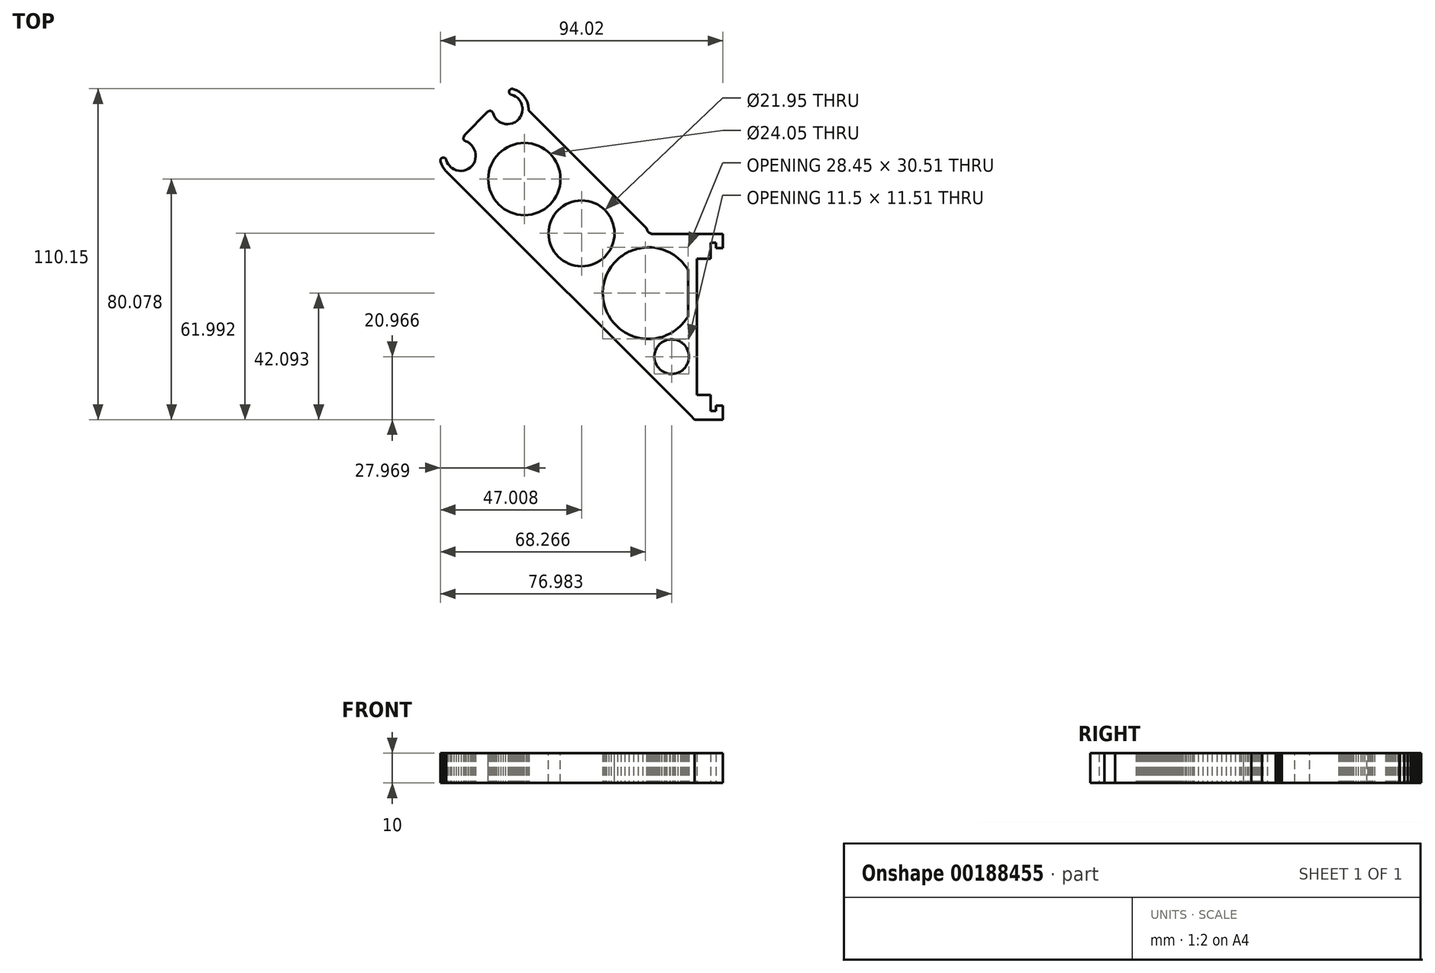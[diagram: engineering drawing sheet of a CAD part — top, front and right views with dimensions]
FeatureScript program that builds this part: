
annotation { "Feature Type Name" : "Feature", "Feature Type Description" : "" }
export const myFeature = defineFeature(function(context is Context, id is Id, definition is map)
    precondition{}
    {
        {
            var Q0;
            Q0=qCreatedBy(makeId("Top.planeOp"),FACE);
            var sketch = newSketch(context, id + "F0", { "sketchPlane" : qUnion([Q0])});
            skLineSegment(sketch, "E0", {"start": v(3.2, -2.47) * mm, "end": v(3.28, -2.4) * mm});
            skLineSegment(sketch, "E1", {"start": v(3.28, -2.4) * mm, "end": v(3.32, -2.36) * mm});
            skLineSegment(sketch, "E2", {"start": v(3.32, -2.36) * mm, "end": v(3.4, -2.28) * mm});
            skLineSegment(sketch, "E3", {"start": v(3.4, -2.28) * mm, "end": v(3.42, -2.25) * mm});
            skLineSegment(sketch, "E4", {"start": v(3.42, -2.25) * mm, "end": v(3.49, -2.16) * mm});
            skLineSegment(sketch, "E5", {"start": v(3.49, -2.16) * mm, "end": v(3.52, -2.12) * mm});
            skLineSegment(sketch, "E6", {"start": v(3.52, -2.12) * mm, "end": v(3.54, -2.07) * mm});
            skLineSegment(sketch, "E7", {"start": v(3.54, -2.07) * mm, "end": v(3.55, -2.06) * mm});
            skLineSegment(sketch, "E8", {"start": v(3.55, -2.06) * mm, "end": v(3.55, -2.03) * mm});
            skLineSegment(sketch, "E9", {"start": v(3.55, -2.03) * mm, "end": v(3.55, -1.98) * mm});
            skLineSegment(sketch, "E10", {"start": v(3.55, -1.98) * mm, "end": v(3.55, -1.8) * mm});
            skLineSegment(sketch, "E11", {"start": v(3.55, -1.8) * mm, "end": v(3.55, -1.76) * mm});
            skLineSegment(sketch, "E12", {"start": v(3.55, -1.76) * mm, "end": v(3.55, -1.72) * mm});
            skLineSegment(sketch, "E13", {"start": v(3.55, -1.72) * mm, "end": v(3.55, -1.7) * mm});
            skLineSegment(sketch, "E14", {"start": v(3.55, -1.7) * mm, "end": v(3.55, -1.66) * mm});
            skLineSegment(sketch, "E15", {"start": v(3.55, -1.66) * mm, "end": v(3.55, -1.65) * mm});
            skLineSegment(sketch, "E16", {"start": v(3.55, -1.65) * mm, "end": v(3.55, -1.63) * mm});
            skLineSegment(sketch, "E17", {"start": v(3.55, -1.63) * mm, "end": v(3.55, -1.62) * mm});
            skLineSegment(sketch, "E18", {"start": v(3.55, -1.62) * mm, "end": v(3.55, -1.62) * mm});
            skLineSegment(sketch, "E19", {"start": v(3.55, -1.62) * mm, "end": v(3.55, -1.56) * mm});
            skLineSegment(sketch, "E20", {"start": v(3.55, -1.56) * mm, "end": v(3.55, -1.56) * mm});
            skLineSegment(sketch, "E21", {"start": v(3.55, -1.56) * mm, "end": v(3.55, -1.55) * mm});
            skLineSegment(sketch, "E22", {"start": v(3.55, -1.55) * mm, "end": v(3.55, -1.48) * mm});
            skLineSegment(sketch, "E23", {"start": v(3.55, -1.48) * mm, "end": v(3.55, -1.42) * mm});
            skLineSegment(sketch, "E24", {"start": v(3.55, -1.42) * mm, "end": v(3.55, -1.36) * mm});
            skLineSegment(sketch, "E25", {"start": v(3.55, -1.36) * mm, "end": v(3.55, -1.2) * mm});
            skLineSegment(sketch, "E26", {"start": v(3.55, -1.2) * mm, "end": v(3.55, -1.17) * mm});
            skLineSegment(sketch, "E27", {"start": v(3.55, -1.17) * mm, "end": v(3.55, -0.86) * mm});
            skLineSegment(sketch, "E28", {"start": v(3.55, -0.86) * mm, "end": v(3.55, -0.53) * mm});
            skLineSegment(sketch, "E29", {"start": v(3.55, -0.53) * mm, "end": v(3.53, -0.5) * mm});
            skLineSegment(sketch, "E30", {"start": v(3.53, -0.5) * mm, "end": v(3.52, -0.48) * mm});
            skLineSegment(sketch, "E31", {"start": v(3.52, -0.48) * mm, "end": v(3.46, -0.4) * mm});
            skLineSegment(sketch, "E32", {"start": v(3.46, -0.4) * mm, "end": v(3.42, -0.35) * mm});
            skLineSegment(sketch, "E33", {"start": v(3.42, -0.35) * mm, "end": v(3.36, -0.27) * mm});
            skLineSegment(sketch, "E34", {"start": v(3.36, -0.27) * mm, "end": v(3.32, -0.23) * mm});
            skLineSegment(sketch, "E35", {"start": v(3.32, -0.23) * mm, "end": v(3.24, -0.16) * mm});
            skLineSegment(sketch, "E36", {"start": v(3.24, -0.16) * mm, "end": v(3.2, -0.13) * mm});
            skLineSegment(sketch, "E37", {"start": v(3.2, -0.13) * mm, "end": v(3.12, -0.06) * mm});
            skLineSegment(sketch, "E38", {"start": v(3.12, -0.06) * mm, "end": v(3.08, -0.03) * mm});
            skLineSegment(sketch, "E39", {"start": v(3.08, -0.03) * mm, "end": v(2.99, 0.02) * mm});
            skLineSegment(sketch, "E40", {"start": v(2.99, 0.02) * mm, "end": v(2.95, 0.05) * mm});
            skLineSegment(sketch, "E41", {"start": v(2.95, 0.05) * mm, "end": v(2.85, 0.1) * mm});
            skLineSegment(sketch, "E42", {"start": v(2.85, 0.1) * mm, "end": v(2.8, 0.12) * mm});
            skLineSegment(sketch, "E43", {"start": v(2.8, 0.12) * mm, "end": v(2.7, 0.15) * mm});
            skLineSegment(sketch, "E44", {"start": v(2.7, 0.15) * mm, "end": v(2.65, 0.17) * mm});
            skLineSegment(sketch, "E45", {"start": v(2.65, 0.17) * mm, "end": v(2.55, 0.2) * mm});
            skLineSegment(sketch, "E46", {"start": v(2.55, 0.2) * mm, "end": v(2.5, 0.2) * mm});
            skLineSegment(sketch, "E47", {"start": v(2.5, 0.2) * mm, "end": v(2.4, 0.22) * mm});
            skLineSegment(sketch, "E48", {"start": v(2.4, 0.22) * mm, "end": v(2.35, 0.22) * mm});
            skLineSegment(sketch, "E49", {"start": v(2.35, 0.22) * mm, "end": v(2.24, 0.23) * mm});
            skLineSegment(sketch, "E50", {"start": v(2.24, 0.23) * mm, "end": v(2.19, 0.23) * mm});
            skLineSegment(sketch, "E51", {"start": v(2.19, 0.23) * mm, "end": v(2.08, 0.22) * mm});
            skLineSegment(sketch, "E52", {"start": v(2.08, 0.22) * mm, "end": v(2.03, 0.22) * mm});
            skLineSegment(sketch, "E53", {"start": v(2.03, 0.22) * mm, "end": v(1.93, 0.2) * mm});
            skLineSegment(sketch, "E54", {"start": v(1.93, 0.2) * mm, "end": v(1.88, 0.19) * mm});
            skLineSegment(sketch, "E55", {"start": v(1.88, 0.19) * mm, "end": v(1.78, 0.16) * mm});
            skLineSegment(sketch, "E56", {"start": v(1.78, 0.16) * mm, "end": v(1.73, 0.14) * mm});
            skLineSegment(sketch, "E57", {"start": v(1.73, 0.14) * mm, "end": v(1.63, 0.1) * mm});
            skLineSegment(sketch, "E58", {"start": v(1.63, 0.1) * mm, "end": v(1.58, 0.08) * mm});
            skLineSegment(sketch, "E59", {"start": v(1.58, 0.08) * mm, "end": v(1.49, 0.03) * mm});
            skLineSegment(sketch, "E60", {"start": v(1.49, 0.03) * mm, "end": v(1.44, 0) * mm});
            skLineSegment(sketch, "E61", {"start": v(1.44, 0) * mm, "end": v(1.36, -0.05) * mm});
            skLineSegment(sketch, "E62", {"start": v(1.36, -0.05) * mm, "end": v(1.31, -0.08) * mm});
            skLineSegment(sketch, "E63", {"start": v(1.31, -0.08) * mm, "end": v(1.23, -0.15) * mm});
            skLineSegment(sketch, "E64", {"start": v(1.23, -0.15) * mm, "end": v(1.2, -0.18) * mm});
            skLineSegment(sketch, "E65", {"start": v(1.2, -0.18) * mm, "end": v(1.12, -0.25) * mm});
            skLineSegment(sketch, "E66", {"start": v(1.12, -0.25) * mm, "end": v(1.08, -0.3) * mm});
            skLineSegment(sketch, "E67", {"start": v(1.08, -0.3) * mm, "end": v(1.02, -0.37) * mm});
            skLineSegment(sketch, "E68", {"start": v(1.02, -0.37) * mm, "end": v(0.99, -0.41) * mm});
            skLineSegment(sketch, "E69", {"start": v(0.99, -0.41) * mm, "end": v(0.93, -0.5) * mm});
            skLineSegment(sketch, "E70", {"start": v(0.93, -0.5) * mm, "end": v(0.9, -0.55) * mm});
            skLineSegment(sketch, "E71", {"start": v(0.9, -0.55) * mm, "end": v(0.85, -0.64) * mm});
            skLineSegment(sketch, "E72", {"start": v(0.85, -0.64) * mm, "end": v(0.83, -0.69) * mm});
            skLineSegment(sketch, "E73", {"start": v(0.83, -0.69) * mm, "end": v(0.8, -0.79) * mm});
            skLineSegment(sketch, "E74", {"start": v(0.8, -0.79) * mm, "end": v(0.78, -0.83) * mm});
            skLineSegment(sketch, "E75", {"start": v(0.78, -0.83) * mm, "end": v(0.75, -0.94) * mm});
            skLineSegment(sketch, "E76", {"start": v(0.75, -0.94) * mm, "end": v(0.74, -0.99) * mm});
            skLineSegment(sketch, "E77", {"start": v(0.74, -0.99) * mm, "end": v(0.72, -1.1) * mm});
            skLineSegment(sketch, "E78", {"start": v(0.72, -1.1) * mm, "end": v(0.71, -1.14) * mm});
            skLineSegment(sketch, "E79", {"start": v(0.71, -1.14) * mm, "end": v(0.7, -1.25) * mm});
            skLineSegment(sketch, "E80", {"start": v(0.7, -1.25) * mm, "end": v(0.7, -1.3) * mm});
            skLineSegment(sketch, "E81", {"start": v(0.7, -1.3) * mm, "end": v(0.7, -1.4) * mm});
            skLineSegment(sketch, "E82", {"start": v(0.7, -1.4) * mm, "end": v(0.71, -1.46) * mm});
            skLineSegment(sketch, "E83", {"start": v(0.71, -1.46) * mm, "end": v(0.73, -1.56) * mm});
            skLineSegment(sketch, "E84", {"start": v(0.73, -1.56) * mm, "end": v(0.74, -1.61) * mm});
            skLineSegment(sketch, "E85", {"start": v(0.74, -1.61) * mm, "end": v(0.76, -1.71) * mm});
            skLineSegment(sketch, "E86", {"start": v(0.76, -1.71) * mm, "end": v(0.78, -1.76) * mm});
            skLineSegment(sketch, "E87", {"start": v(0.78, -1.76) * mm, "end": v(0.81, -1.86) * mm});
            skLineSegment(sketch, "E88", {"start": v(0.81, -1.86) * mm, "end": v(0.83, -1.9) * mm});
            skLineSegment(sketch, "E89", {"start": v(0.83, -1.9) * mm, "end": v(0.88, -2) * mm});
            skLineSegment(sketch, "E90", {"start": v(0.88, -2) * mm, "end": v(0.9, -2.05) * mm});
            skLineSegment(sketch, "E91", {"start": v(0.9, -2.05) * mm, "end": v(0.96, -2.14) * mm});
            skLineSegment(sketch, "E92", {"start": v(0.96, -2.14) * mm, "end": v(0.99, -2.18) * mm});
            skLineSegment(sketch, "E93", {"start": v(0.99, -2.18) * mm, "end": v(1.05, -2.26) * mm});
            skLineSegment(sketch, "E94", {"start": v(1.05, -2.26) * mm, "end": v(1.08, -2.3) * mm});
            skLineSegment(sketch, "E95", {"start": v(1.08, -2.3) * mm, "end": v(1.16, -2.38) * mm});
            skLineSegment(sketch, "E96", {"start": v(1.16, -2.38) * mm, "end": v(1.2, -2.42) * mm});
            skLineSegment(sketch, "E97", {"start": v(1.2, -2.42) * mm, "end": v(1.27, -2.49) * mm});
            skLineSegment(sketch, "E98", {"start": v(1.27, -2.49) * mm, "end": v(1.31, -2.52) * mm});
            skLineSegment(sketch, "E99", {"start": v(1.31, -2.52) * mm, "end": v(1.4, -2.58) * mm});
            skLineSegment(sketch, "E100", {"start": v(1.4, -2.58) * mm, "end": v(1.44, -2.6) * mm});
            skLineSegment(sketch, "E101", {"start": v(1.44, -2.6) * mm, "end": v(1.54, -2.66) * mm});
            skLineSegment(sketch, "E102", {"start": v(1.54, -2.66) * mm, "end": v(1.58, -2.68) * mm});
            skLineSegment(sketch, "E103", {"start": v(1.58, -2.68) * mm, "end": v(1.68, -2.72) * mm});
            skLineSegment(sketch, "E104", {"start": v(1.68, -2.72) * mm, "end": v(1.73, -2.74) * mm});
            skLineSegment(sketch, "E105", {"start": v(1.73, -2.74) * mm, "end": v(1.83, -2.77) * mm});
            skLineSegment(sketch, "E106", {"start": v(1.83, -2.77) * mm, "end": v(1.88, -2.78) * mm});
            skLineSegment(sketch, "E107", {"start": v(1.88, -2.78) * mm, "end": v(1.98, -2.8) * mm});
            skLineSegment(sketch, "E108", {"start": v(1.98, -2.8) * mm, "end": v(2.03, -2.81) * mm});
            skLineSegment(sketch, "E109", {"start": v(2.03, -2.81) * mm, "end": v(2.14, -2.82) * mm});
            skLineSegment(sketch, "E110", {"start": v(2.14, -2.82) * mm, "end": v(2.19, -2.82) * mm});
            skLineSegment(sketch, "E111", {"start": v(2.19, -2.82) * mm, "end": v(2.3, -2.82) * mm});
            skLineSegment(sketch, "E112", {"start": v(2.3, -2.82) * mm, "end": v(2.35, -2.82) * mm});
            skLineSegment(sketch, "E113", {"start": v(2.35, -2.82) * mm, "end": v(2.45, -2.8) * mm});
            skLineSegment(sketch, "E114", {"start": v(2.45, -2.8) * mm, "end": v(2.5, -2.8) * mm});
            skLineSegment(sketch, "E115", {"start": v(2.5, -2.8) * mm, "end": v(2.6, -2.78) * mm});
            skLineSegment(sketch, "E116", {"start": v(2.6, -2.78) * mm, "end": v(2.65, -2.76) * mm});
            skLineSegment(sketch, "E117", {"start": v(2.65, -2.76) * mm, "end": v(2.75, -2.73) * mm});
            skLineSegment(sketch, "E118", {"start": v(2.75, -2.73) * mm, "end": v(2.8, -2.71) * mm});
            skLineSegment(sketch, "E119", {"start": v(2.8, -2.71) * mm, "end": v(2.9, -2.67) * mm});
            skLineSegment(sketch, "E120", {"start": v(2.9, -2.67) * mm, "end": v(2.95, -2.65) * mm});
            skLineSegment(sketch, "E121", {"start": v(2.95, -2.65) * mm, "end": v(3.04, -2.6) * mm});
            skLineSegment(sketch, "E122", {"start": v(3.04, -2.6) * mm, "end": v(3.08, -2.56) * mm});
            skLineSegment(sketch, "E123", {"start": v(3.08, -2.56) * mm, "end": v(3.16, -2.5) * mm});
            skLineSegment(sketch, "E124", {"start": v(3.16, -2.5) * mm, "end": v(3.2, -2.47) * mm});
            skLineSegment(sketch, "E125", {"start": v(2.16, 0.86) * mm, "end": v(2.17, 0.83) * mm});
            skLineSegment(sketch, "E126", {"start": v(2.17, 0.83) * mm, "end": v(2.17, 0.83) * mm});
            skLineSegment(sketch, "E127", {"start": v(2.17, 0.83) * mm, "end": v(2.18, 0.8) * mm});
            skLineSegment(sketch, "E128", {"start": v(2.18, 0.8) * mm, "end": v(2.19, 0.8) * mm});
            skLineSegment(sketch, "E129", {"start": v(2.19, 0.8) * mm, "end": v(2.2, 0.76) * mm});
            skLineSegment(sketch, "E130", {"start": v(2.2, 0.76) * mm, "end": v(2.2, 0.76) * mm});
            skLineSegment(sketch, "E131", {"start": v(2.2, 0.76) * mm, "end": v(2.23, 0.74) * mm});
            skLineSegment(sketch, "E132", {"start": v(2.23, 0.74) * mm, "end": v(2.23, 0.73) * mm});
            skLineSegment(sketch, "E133", {"start": v(2.23, 0.73) * mm, "end": v(2.25, 0.71) * mm});
            skLineSegment(sketch, "E134", {"start": v(2.25, 0.71) * mm, "end": v(2.26, 0.71) * mm});
            skLineSegment(sketch, "E135", {"start": v(2.26, 0.71) * mm, "end": v(2.29, 0.7) * mm});
            skLineSegment(sketch, "E136", {"start": v(2.29, 0.7) * mm, "end": v(2.29, 0.7) * mm});
            skLineSegment(sketch, "E137", {"start": v(2.29, 0.7) * mm, "end": v(2.32, 0.68) * mm});
            skLineSegment(sketch, "E138", {"start": v(2.32, 0.68) * mm, "end": v(2.32, 0.68) * mm});
            skLineSegment(sketch, "E139", {"start": v(2.32, 0.68) * mm, "end": v(2.35, 0.67) * mm});
            skLineSegment(sketch, "E140", {"start": v(2.35, 0.67) * mm, "end": v(2.36, 0.67) * mm});
            skLineSegment(sketch, "E141", {"start": v(2.36, 0.67) * mm, "end": v(2.4, 0.67) * mm});
            skLineSegment(sketch, "E142", {"start": v(2.4, 0.67) * mm, "end": v(2.47, 0.67) * mm});
            skLineSegment(sketch, "E143", {"start": v(2.47, 0.67) * mm, "end": v(4.7, 0.67) * mm});
            skLineSegment(sketch, "E144", {"start": v(4.7, 0.67) * mm, "end": v(4.7, 0.65) * mm});
            skLineSegment(sketch, "E145", {"start": v(4.7, 0.65) * mm, "end": v(4.7, 0.2) * mm});
            skLineSegment(sketch, "E146", {"start": v(4.7, 0.2) * mm, "end": v(4.7, 0.2) * mm});
            skLineSegment(sketch, "E147", {"start": v(4.7, 0.2) * mm, "end": v(4.48, 0.2) * mm});
            skLineSegment(sketch, "E148", {"start": v(4.48, 0.2) * mm, "end": v(4.48, 0.21) * mm});
            skLineSegment(sketch, "E149", {"start": v(4.48, 0.21) * mm, "end": v(4.48, 0.38) * mm});
            skLineSegment(sketch, "E150", {"start": v(4.48, 0.38) * mm, "end": v(4.47, 0.38) * mm});
            skLineSegment(sketch, "E151", {"start": v(4.47, 0.38) * mm, "end": v(4.3, 0.38) * mm});
            skLineSegment(sketch, "E152", {"start": v(4.3, 0.38) * mm, "end": v(4.3, 0.36) * mm});
            skLineSegment(sketch, "E153", {"start": v(4.3, 0.36) * mm, "end": v(4.3, 0.18) * mm});
            skLineSegment(sketch, "E154", {"start": v(4.3, 0.18) * mm, "end": v(4.3, -0.15) * mm});
            skLineSegment(sketch, "E155", {"start": v(4.3, -0.15) * mm, "end": v(3.97, -0.15) * mm});
            skLineSegment(sketch, "E156", {"start": v(3.97, -0.15) * mm, "end": v(3.83, -0.15) * mm});
            skLineSegment(sketch, "E157", {"start": v(3.83, -0.15) * mm, "end": v(3.83, -3.22) * mm});
            skLineSegment(sketch, "E158", {"start": v(3.83, -3.22) * mm, "end": v(3.83, -4.69) * mm});
            skLineSegment(sketch, "E159", {"start": v(3.83, -4.69) * mm, "end": v(4.17, -4.69) * mm});
            skLineSegment(sketch, "E160", {"start": v(4.17, -4.69) * mm, "end": v(4.3, -4.69) * mm});
            skLineSegment(sketch, "E161", {"start": v(4.3, -4.69) * mm, "end": v(4.3, -5.02) * mm});
            skLineSegment(sketch, "E162", {"start": v(4.3, -5.02) * mm, "end": v(4.3, -5.2) * mm});
            skLineSegment(sketch, "E163", {"start": v(4.3, -5.2) * mm, "end": v(4.3, -5.22) * mm});
            skLineSegment(sketch, "E164", {"start": v(4.3, -5.22) * mm, "end": v(4.3, -5.22) * mm});
            skLineSegment(sketch, "E165", {"start": v(4.3, -5.22) * mm, "end": v(4.48, -5.22) * mm});
            skLineSegment(sketch, "E166", {"start": v(4.48, -5.22) * mm, "end": v(4.48, -5.21) * mm});
            skLineSegment(sketch, "E167", {"start": v(4.48, -5.21) * mm, "end": v(4.48, -5.04) * mm});
            skLineSegment(sketch, "E168", {"start": v(4.48, -5.04) * mm, "end": v(4.48, -5.04) * mm});
            skLineSegment(sketch, "E169", {"start": v(4.48, -5.04) * mm, "end": v(4.7, -5.04) * mm});
            skLineSegment(sketch, "E170", {"start": v(4.7, -5.04) * mm, "end": v(4.7, -5.06) * mm});
            skLineSegment(sketch, "E171", {"start": v(4.7, -5.06) * mm, "end": v(4.7, -5.5) * mm});
            skLineSegment(sketch, "E172", {"start": v(4.7, -5.5) * mm, "end": v(4.67, -5.5) * mm});
            skLineSegment(sketch, "E173", {"start": v(4.67, -5.5) * mm, "end": v(3.76, -5.5) * mm});
            skLineSegment(sketch, "E174", {"start": v(3.76, -5.5) * mm, "end": v(3.62, -5.36) * mm});
            skLineSegment(sketch, "E175", {"start": v(3.62, -5.36) * mm, "end": v(-4.5, 2.76) * mm});
            skLineSegment(sketch, "E176", {"start": v(2.42, -3.38) * mm, "end": v(2.43, -3.32) * mm});
            skLineSegment(sketch, "E177", {"start": v(2.43, -3.32) * mm, "end": v(2.44, -3.29) * mm});
            skLineSegment(sketch, "E178", {"start": v(2.44, -3.29) * mm, "end": v(2.45, -3.23) * mm});
            skLineSegment(sketch, "E179", {"start": v(2.45, -3.23) * mm, "end": v(2.46, -3.2) * mm});
            skLineSegment(sketch, "E180", {"start": v(2.46, -3.2) * mm, "end": v(2.49, -3.14) * mm});
            skLineSegment(sketch, "E181", {"start": v(2.49, -3.14) * mm, "end": v(2.5, -3.12) * mm});
            skLineSegment(sketch, "E182", {"start": v(2.5, -3.12) * mm, "end": v(2.54, -3.06) * mm});
            skLineSegment(sketch, "E183", {"start": v(2.54, -3.06) * mm, "end": v(2.56, -3.04) * mm});
            skLineSegment(sketch, "E184", {"start": v(2.56, -3.04) * mm, "end": v(2.6, -3) * mm});
            skLineSegment(sketch, "E185", {"start": v(2.6, -3) * mm, "end": v(2.62, -2.98) * mm});
            skLineSegment(sketch, "E186", {"start": v(2.62, -2.98) * mm, "end": v(2.67, -2.94) * mm});
            skLineSegment(sketch, "E187", {"start": v(2.67, -2.94) * mm, "end": v(2.7, -2.92) * mm});
            skLineSegment(sketch, "E188", {"start": v(2.7, -2.92) * mm, "end": v(2.75, -2.9) * mm});
            skLineSegment(sketch, "E189", {"start": v(2.75, -2.9) * mm, "end": v(2.78, -2.88) * mm});
            skLineSegment(sketch, "E190", {"start": v(2.78, -2.88) * mm, "end": v(2.84, -2.86) * mm});
            skLineSegment(sketch, "E191", {"start": v(2.84, -2.86) * mm, "end": v(2.87, -2.85) * mm});
            skLineSegment(sketch, "E192", {"start": v(2.87, -2.85) * mm, "end": v(2.93, -2.84) * mm});
            skLineSegment(sketch, "E193", {"start": v(2.93, -2.84) * mm, "end": v(2.96, -2.84) * mm});
            skLineSegment(sketch, "E194", {"start": v(2.96, -2.84) * mm, "end": v(3.02, -2.84) * mm});
            skLineSegment(sketch, "E195", {"start": v(3.02, -2.84) * mm, "end": v(3.05, -2.84) * mm});
            skLineSegment(sketch, "E196", {"start": v(3.05, -2.84) * mm, "end": v(3.11, -2.85) * mm});
            skLineSegment(sketch, "E197", {"start": v(3.11, -2.85) * mm, "end": v(3.14, -2.86) * mm});
            skLineSegment(sketch, "E198", {"start": v(3.14, -2.86) * mm, "end": v(3.2, -2.87) * mm});
            skLineSegment(sketch, "E199", {"start": v(3.2, -2.87) * mm, "end": v(3.23, -2.89) * mm});
            skLineSegment(sketch, "E200", {"start": v(3.23, -2.89) * mm, "end": v(3.29, -2.91) * mm});
            skLineSegment(sketch, "E201", {"start": v(3.29, -2.91) * mm, "end": v(3.31, -2.93) * mm});
            skLineSegment(sketch, "E202", {"start": v(3.31, -2.93) * mm, "end": v(3.36, -2.96) * mm});
            skLineSegment(sketch, "E203", {"start": v(3.36, -2.96) * mm, "end": v(3.38, -2.99) * mm});
            skLineSegment(sketch, "E204", {"start": v(3.38, -2.99) * mm, "end": v(3.43, -3.03) * mm});
            skLineSegment(sketch, "E205", {"start": v(3.43, -3.03) * mm, "end": v(3.45, -3.05) * mm});
            skLineSegment(sketch, "E206", {"start": v(3.45, -3.05) * mm, "end": v(3.49, -3.1) * mm});
            skLineSegment(sketch, "E207", {"start": v(3.49, -3.1) * mm, "end": v(3.5, -3.13) * mm});
            skLineSegment(sketch, "E208", {"start": v(3.5, -3.13) * mm, "end": v(3.53, -3.19) * mm});
            skLineSegment(sketch, "E209", {"start": v(3.53, -3.19) * mm, "end": v(3.54, -3.21) * mm});
            skLineSegment(sketch, "E210", {"start": v(3.54, -3.21) * mm, "end": v(3.56, -3.27) * mm});
            skLineSegment(sketch, "E211", {"start": v(3.56, -3.27) * mm, "end": v(3.56, -3.3) * mm});
            skLineSegment(sketch, "E212", {"start": v(3.56, -3.3) * mm, "end": v(3.57, -3.36) * mm});
            skLineSegment(sketch, "E213", {"start": v(3.57, -3.36) * mm, "end": v(3.57, -3.4) * mm});
            skLineSegment(sketch, "E214", {"start": v(3.57, -3.4) * mm, "end": v(3.57, -3.46) * mm});
            skLineSegment(sketch, "E215", {"start": v(3.57, -3.46) * mm, "end": v(3.57, -3.49) * mm});
            skLineSegment(sketch, "E216", {"start": v(3.57, -3.49) * mm, "end": v(3.56, -3.55) * mm});
            skLineSegment(sketch, "E217", {"start": v(3.56, -3.55) * mm, "end": v(3.55, -3.58) * mm});
            skLineSegment(sketch, "E218", {"start": v(3.55, -3.58) * mm, "end": v(3.53, -3.64) * mm});
            skLineSegment(sketch, "E219", {"start": v(3.53, -3.64) * mm, "end": v(3.51, -3.66) * mm});
            skLineSegment(sketch, "E220", {"start": v(3.51, -3.66) * mm, "end": v(3.49, -3.72) * mm});
            skLineSegment(sketch, "E221", {"start": v(3.49, -3.72) * mm, "end": v(3.47, -3.74) * mm});
            skLineSegment(sketch, "E222", {"start": v(3.47, -3.74) * mm, "end": v(3.43, -3.8) * mm});
            skLineSegment(sketch, "E223", {"start": v(3.43, -3.8) * mm, "end": v(3.4, -3.81) * mm});
            skLineSegment(sketch, "E224", {"start": v(3.4, -3.81) * mm, "end": v(3.36, -3.86) * mm});
            skLineSegment(sketch, "E225", {"start": v(3.36, -3.86) * mm, "end": v(3.34, -3.87) * mm});
            skLineSegment(sketch, "E226", {"start": v(3.34, -3.87) * mm, "end": v(3.29, -3.9) * mm});
            skLineSegment(sketch, "E227", {"start": v(3.29, -3.9) * mm, "end": v(3.26, -3.92) * mm});
            skLineSegment(sketch, "E228", {"start": v(3.26, -3.92) * mm, "end": v(3.2, -3.95) * mm});
            skLineSegment(sketch, "E229", {"start": v(3.2, -3.95) * mm, "end": v(3.17, -3.96) * mm});
            skLineSegment(sketch, "E230", {"start": v(3.17, -3.96) * mm, "end": v(3.11, -3.98) * mm});
            skLineSegment(sketch, "E231", {"start": v(3.11, -3.98) * mm, "end": v(3.08, -3.98) * mm});
            skLineSegment(sketch, "E232", {"start": v(3.08, -3.98) * mm, "end": v(3.02, -3.99) * mm});
            skLineSegment(sketch, "E233", {"start": v(3.02, -3.99) * mm, "end": v(3, -3.99) * mm});
            skLineSegment(sketch, "E234", {"start": v(3, -3.99) * mm, "end": v(2.93, -3.98) * mm});
            skLineSegment(sketch, "E235", {"start": v(2.93, -3.98) * mm, "end": v(2.9, -3.98) * mm});
            skLineSegment(sketch, "E236", {"start": v(2.9, -3.98) * mm, "end": v(2.84, -3.96) * mm});
            skLineSegment(sketch, "E237", {"start": v(2.84, -3.96) * mm, "end": v(2.8, -3.95) * mm});
            skLineSegment(sketch, "E238", {"start": v(2.8, -3.95) * mm, "end": v(2.75, -3.93) * mm});
            skLineSegment(sketch, "E239", {"start": v(2.75, -3.93) * mm, "end": v(2.73, -3.92) * mm});
            skLineSegment(sketch, "E240", {"start": v(2.73, -3.92) * mm, "end": v(2.67, -3.88) * mm});
            skLineSegment(sketch, "E241", {"start": v(2.67, -3.88) * mm, "end": v(2.65, -3.87) * mm});
            skLineSegment(sketch, "E242", {"start": v(2.65, -3.87) * mm, "end": v(2.6, -3.83) * mm});
            skLineSegment(sketch, "E243", {"start": v(2.6, -3.83) * mm, "end": v(2.58, -3.8) * mm});
            skLineSegment(sketch, "E244", {"start": v(2.58, -3.8) * mm, "end": v(2.54, -3.76) * mm});
            skLineSegment(sketch, "E245", {"start": v(2.54, -3.76) * mm, "end": v(2.52, -3.73) * mm});
            skLineSegment(sketch, "E246", {"start": v(2.52, -3.73) * mm, "end": v(2.49, -3.68) * mm});
            skLineSegment(sketch, "E247", {"start": v(2.49, -3.68) * mm, "end": v(2.48, -3.65) * mm});
            skLineSegment(sketch, "E248", {"start": v(2.48, -3.65) * mm, "end": v(2.45, -3.6) * mm});
            skLineSegment(sketch, "E249", {"start": v(2.45, -3.6) * mm, "end": v(2.44, -3.56) * mm});
            skLineSegment(sketch, "E250", {"start": v(2.44, -3.56) * mm, "end": v(2.43, -3.5) * mm});
            skLineSegment(sketch, "E251", {"start": v(2.43, -3.5) * mm, "end": v(2.43, -3.47) * mm});
            skLineSegment(sketch, "E252", {"start": v(2.43, -3.47) * mm, "end": v(2.42, -3.41) * mm});
            skLineSegment(sketch, "E253", {"start": v(2.42, -3.41) * mm, "end": v(2.42, -3.38) * mm});
            skLineSegment(sketch, "E254", {"start": v(2.16, 0.87) * mm, "end": v(-1.75, 4.77) * mm});
            skLineSegment(sketch, "E255", {"start": v(2.16, 0.87) * mm, "end": v(2.16, 0.86) * mm});
            skLineSegment(sketch, "E256", {"start": v(-3.53, 3.17) * mm, "end": v(-3.53, 3.17) * mm});
            skLineSegment(sketch, "E257", {"start": v(-3.53, 3.17) * mm, "end": v(-3.52, 3.25) * mm});
            skLineSegment(sketch, "E258", {"start": v(-3.52, 3.25) * mm, "end": v(-3.52, 3.25) * mm});
            skLineSegment(sketch, "E259", {"start": v(-3.52, 3.25) * mm, "end": v(-3.53, 3.33) * mm});
            skLineSegment(sketch, "E260", {"start": v(-3.53, 3.33) * mm, "end": v(-3.53, 3.33) * mm});
            skLineSegment(sketch, "E261", {"start": v(-3.53, 3.33) * mm, "end": v(-3.54, 3.41) * mm});
            skLineSegment(sketch, "E262", {"start": v(-3.54, 3.41) * mm, "end": v(-3.54, 3.42) * mm});
            skLineSegment(sketch, "E263", {"start": v(-3.54, 3.42) * mm, "end": v(-3.57, 3.5) * mm});
            skLineSegment(sketch, "E264", {"start": v(-3.57, 3.5) * mm, "end": v(-3.57, 3.5) * mm});
            skLineSegment(sketch, "E265", {"start": v(-3.57, 3.5) * mm, "end": v(-3.61, 3.56) * mm});
            skLineSegment(sketch, "E266", {"start": v(-3.61, 3.56) * mm, "end": v(-3.62, 3.56) * mm});
            skLineSegment(sketch, "E267", {"start": v(-3.62, 3.56) * mm, "end": v(-3.67, 3.63) * mm});
            skLineSegment(sketch, "E268", {"start": v(-3.67, 3.63) * mm, "end": v(-3.68, 3.64) * mm});
            skLineSegment(sketch, "E269", {"start": v(-3.68, 3.64) * mm, "end": v(-3.75, 3.7) * mm});
            skLineSegment(sketch, "E270", {"start": v(-3.9, 3.96) * mm, "end": v(-3.12, 4.74) * mm});
            skLineSegment(sketch, "E271", {"start": v(-3.12, 4.74) * mm, "end": v(-3.1, 4.75) * mm});
            skLineSegment(sketch, "E272", {"start": v(-3.1, 4.75) * mm, "end": v(-3.1, 4.76) * mm});
            skLineSegment(sketch, "E273", {"start": v(-3.1, 4.76) * mm, "end": v(-3.08, 4.77) * mm});
            skLineSegment(sketch, "E274", {"start": v(-3.08, 4.77) * mm, "end": v(-3.06, 4.77) * mm});
            skLineSegment(sketch, "E275", {"start": v(-3.06, 4.77) * mm, "end": v(-3.04, 4.77) * mm});
            skLineSegment(sketch, "E276", {"start": v(-3.04, 4.77) * mm, "end": v(-3.03, 4.77) * mm});
            skLineSegment(sketch, "E277", {"start": v(-3.03, 4.77) * mm, "end": v(-3.01, 4.77) * mm});
            skLineSegment(sketch, "E278", {"start": v(-3.01, 4.77) * mm, "end": v(-3, 4.76) * mm});
            skLineSegment(sketch, "E279", {"start": v(-3, 4.76) * mm, "end": v(-2.98, 4.75) * mm});
            skLineSegment(sketch, "E280", {"start": v(-2.98, 4.75) * mm, "end": v(-2.97, 4.74) * mm});
            skLineSegment(sketch, "E281", {"start": v(-2.97, 4.74) * mm, "end": v(-2.96, 4.73) * mm});
            skLineSegment(sketch, "E282", {"start": v(-2.96, 4.73) * mm, "end": v(-2.95, 4.71) * mm});
            skLineSegment(sketch, "E283", {"start": v(-2.95, 4.71) * mm, "end": v(-2.95, 4.7) * mm});
            skLineSegment(sketch, "E284", {"start": v(-2.95, 4.7) * mm, "end": v(-2.95, 4.7) * mm});
            skLineSegment(sketch, "E285", {"start": v(-2.95, 4.7) * mm, "end": v(-2.92, 4.62) * mm});
            skLineSegment(sketch, "E286", {"start": v(-2.92, 4.62) * mm, "end": v(-2.92, 4.62) * mm});
            skLineSegment(sketch, "E287", {"start": v(-2.92, 4.62) * mm, "end": v(-2.88, 4.55) * mm});
            skLineSegment(sketch, "E288", {"start": v(-2.88, 4.55) * mm, "end": v(-2.88, 4.54) * mm});
            skLineSegment(sketch, "E289", {"start": v(-2.88, 4.54) * mm, "end": v(-2.83, 4.48) * mm});
            skLineSegment(sketch, "E290", {"start": v(-2.83, 4.48) * mm, "end": v(-2.83, 4.48) * mm});
            skLineSegment(sketch, "E291", {"start": v(-2.83, 4.48) * mm, "end": v(-2.76, 4.43) * mm});
            skLineSegment(sketch, "E292", {"start": v(-2.76, 4.43) * mm, "end": v(-2.76, 4.42) * mm});
            skLineSegment(sketch, "E293", {"start": v(-2.76, 4.42) * mm, "end": v(-2.7, 4.38) * mm});
            skLineSegment(sketch, "E294", {"start": v(-2.7, 4.38) * mm, "end": v(-2.7, 4.38) * mm});
            skLineSegment(sketch, "E295", {"start": v(-2.7, 4.38) * mm, "end": v(-2.62, 4.35) * mm});
            skLineSegment(sketch, "E296", {"start": v(-2.62, 4.35) * mm, "end": v(-2.61, 4.35) * mm});
            skLineSegment(sketch, "E297", {"start": v(-2.61, 4.35) * mm, "end": v(-2.53, 4.33) * mm});
            skLineSegment(sketch, "E298", {"start": v(-2.53, 4.33) * mm, "end": v(-2.53, 4.33) * mm});
            skLineSegment(sketch, "E299", {"start": v(-2.53, 4.33) * mm, "end": v(-2.45, 4.33) * mm});
            skLineSegment(sketch, "E300", {"start": v(-2.45, 4.33) * mm, "end": v(-2.45, 4.33) * mm});
            skLineSegment(sketch, "E301", {"start": v(-2.45, 4.33) * mm, "end": v(-2.37, 4.34) * mm});
            skLineSegment(sketch, "E302", {"start": v(-2.37, 4.34) * mm, "end": v(-2.36, 4.34) * mm});
            skLineSegment(sketch, "E303", {"start": v(-2.36, 4.34) * mm, "end": v(-2.29, 4.36) * mm});
            skLineSegment(sketch, "E304", {"start": v(-2.29, 4.36) * mm, "end": v(-2.28, 4.36) * mm});
            skLineSegment(sketch, "E305", {"start": v(-2.28, 4.36) * mm, "end": v(-2.21, 4.4) * mm});
            skLineSegment(sketch, "E306", {"start": v(-2.21, 4.4) * mm, "end": v(-2.2, 4.4) * mm});
            skLineSegment(sketch, "E307", {"start": v(-2.2, 4.4) * mm, "end": v(-2.14, 4.45) * mm});
            skLineSegment(sketch, "E308", {"start": v(-2.14, 4.45) * mm, "end": v(-2.14, 4.45) * mm});
            skLineSegment(sketch, "E309", {"start": v(-2.14, 4.45) * mm, "end": v(-2.08, 4.5) * mm});
            skLineSegment(sketch, "E310", {"start": v(-2.08, 4.5) * mm, "end": v(-2.08, 4.5) * mm});
            skLineSegment(sketch, "E311", {"start": v(-2.08, 4.5) * mm, "end": v(-2.04, 4.57) * mm});
            skLineSegment(sketch, "E312", {"start": v(-2.04, 4.57) * mm, "end": v(-2.03, 4.58) * mm});
            skLineSegment(sketch, "E313", {"start": v(-2.03, 4.58) * mm, "end": v(-2, 4.65) * mm});
            skLineSegment(sketch, "E314", {"start": v(-2, 4.65) * mm, "end": v(-2, 4.65) * mm});
            skLineSegment(sketch, "E315", {"start": v(-2, 4.65) * mm, "end": v(-1.98, 4.73) * mm});
            skLineSegment(sketch, "E316", {"start": v(-1.98, 4.73) * mm, "end": v(-1.98, 4.73) * mm});
            skLineSegment(sketch, "E317", {"start": v(-1.98, 4.73) * mm, "end": v(-1.97, 4.81) * mm});
            skLineSegment(sketch, "E318", {"start": v(-1.97, 4.81) * mm, "end": v(-1.97, 4.81) * mm});
            skLineSegment(sketch, "E319", {"start": v(-1.97, 4.81) * mm, "end": v(-1.97, 4.9) * mm});
            skLineSegment(sketch, "E320", {"start": v(-1.97, 4.9) * mm, "end": v(-1.97, 4.9) * mm});
            skLineSegment(sketch, "E321", {"start": v(-1.97, 4.9) * mm, "end": v(-1.99, 4.98) * mm});
            skLineSegment(sketch, "E322", {"start": v(-1.99, 4.98) * mm, "end": v(-2, 4.98) * mm});
            skLineSegment(sketch, "E323", {"start": v(-2, 4.98) * mm, "end": v(-2.02, 5.05) * mm});
            skLineSegment(sketch, "E324", {"start": v(-2.02, 5.05) * mm, "end": v(-2.02, 5.06) * mm});
            skLineSegment(sketch, "E325", {"start": v(-2.02, 5.06) * mm, "end": v(-2.06, 5.13) * mm});
            skLineSegment(sketch, "E326", {"start": v(-2.06, 5.13) * mm, "end": v(-2.07, 5.13) * mm});
            skLineSegment(sketch, "E327", {"start": v(-2.07, 5.13) * mm, "end": v(-2.12, 5.19) * mm});
            skLineSegment(sketch, "E328", {"start": v(-2.12, 5.19) * mm, "end": v(-2.12, 5.2) * mm});
            skLineSegment(sketch, "E329", {"start": v(-2.12, 5.2) * mm, "end": v(-2.19, 5.24) * mm});
            skLineSegment(sketch, "E330", {"start": v(-2.19, 5.24) * mm, "end": v(-2.19, 5.24) * mm});
            skLineSegment(sketch, "E331", {"start": v(-2.19, 5.24) * mm, "end": v(-2.26, 5.28) * mm});
            skLineSegment(sketch, "E332", {"start": v(-2.26, 5.28) * mm, "end": v(-2.26, 5.28) * mm});
            skLineSegment(sketch, "E333", {"start": v(-2.26, 5.28) * mm, "end": v(-2.34, 5.31) * mm});
            skLineSegment(sketch, "E334", {"start": v(-2.34, 5.31) * mm, "end": v(-2.35, 5.32) * mm});
            skLineSegment(sketch, "E335", {"start": v(-2.35, 5.32) * mm, "end": v(-2.37, 5.32) * mm});
            skLineSegment(sketch, "E336", {"start": v(-2.37, 5.32) * mm, "end": v(-2.38, 5.33) * mm});
            skLineSegment(sketch, "E337", {"start": v(-2.38, 5.33) * mm, "end": v(-2.4, 5.35) * mm});
            skLineSegment(sketch, "E338", {"start": v(-2.4, 5.35) * mm, "end": v(-2.4, 5.36) * mm});
            skLineSegment(sketch, "E339", {"start": v(-2.4, 5.36) * mm, "end": v(-2.4, 5.38) * mm});
            skLineSegment(sketch, "E340", {"start": v(-2.4, 5.38) * mm, "end": v(-2.4, 5.4) * mm});
            skLineSegment(sketch, "E341", {"start": v(-2.4, 5.4) * mm, "end": v(-2.41, 5.4) * mm});
            skLineSegment(sketch, "E342", {"start": v(-2.41, 5.4) * mm, "end": v(-2.4, 5.43) * mm});
            skLineSegment(sketch, "E343", {"start": v(-2.4, 5.43) * mm, "end": v(-2.4, 5.44) * mm});
            skLineSegment(sketch, "E344", {"start": v(-2.4, 5.44) * mm, "end": v(-2.4, 5.46) * mm});
            skLineSegment(sketch, "E345", {"start": v(-2.4, 5.46) * mm, "end": v(-2.39, 5.47) * mm});
            skLineSegment(sketch, "E346", {"start": v(-2.39, 5.47) * mm, "end": v(-2.38, 5.48) * mm});
            skLineSegment(sketch, "E347", {"start": v(-2.38, 5.48) * mm, "end": v(-2.36, 5.5) * mm});
            skLineSegment(sketch, "E348", {"start": v(-2.36, 5.5) * mm, "end": v(-2.35, 5.5) * mm});
            skLineSegment(sketch, "E349", {"start": v(-2.35, 5.5) * mm, "end": v(-2.33, 5.5) * mm});
            skLineSegment(sketch, "E350", {"start": v(-2.33, 5.5) * mm, "end": v(-2.32, 5.5) * mm});
            skLineSegment(sketch, "E351", {"start": v(-2.32, 5.5) * mm, "end": v(-2.3, 5.5) * mm});
            skLineSegment(sketch, "E352", {"start": v(-2.3, 5.5) * mm, "end": v(-2.29, 5.5) * mm});
            skLineSegment(sketch, "E353", {"start": v(-2.29, 5.5) * mm, "end": v(-2.28, 5.5) * mm});
            skLineSegment(sketch, "E354", {"start": v(-2.28, 5.5) * mm, "end": v(-2.18, 5.47) * mm});
            skLineSegment(sketch, "E355", {"start": v(-2.18, 5.47) * mm, "end": v(-2.17, 5.46) * mm});
            skLineSegment(sketch, "E356", {"start": v(-2.17, 5.46) * mm, "end": v(-2.08, 5.4) * mm});
            skLineSegment(sketch, "E357", {"start": v(-2.08, 5.4) * mm, "end": v(-2.07, 5.4) * mm});
            skLineSegment(sketch, "E358", {"start": v(-2.07, 5.4) * mm, "end": v(-1.99, 5.34) * mm});
            skLineSegment(sketch, "E359", {"start": v(-1.99, 5.34) * mm, "end": v(-1.99, 5.34) * mm});
            skLineSegment(sketch, "E360", {"start": v(-1.99, 5.34) * mm, "end": v(-1.91, 5.25) * mm});
            skLineSegment(sketch, "E361", {"start": v(-1.91, 5.25) * mm, "end": v(-1.9, 5.25) * mm});
            skLineSegment(sketch, "E362", {"start": v(-1.9, 5.25) * mm, "end": v(-1.85, 5.16) * mm});
            skLineSegment(sketch, "E363", {"start": v(-1.85, 5.16) * mm, "end": v(-1.85, 5.15) * mm});
            skLineSegment(sketch, "E364", {"start": v(-1.85, 5.15) * mm, "end": v(-1.8, 5.05) * mm});
            skLineSegment(sketch, "E365", {"start": v(-1.8, 5.05) * mm, "end": v(-1.8, 5.05) * mm});
            skLineSegment(sketch, "E366", {"start": v(-1.8, 5.05) * mm, "end": v(-1.78, 4.94) * mm});
            skLineSegment(sketch, "E367", {"start": v(-1.78, 4.94) * mm, "end": v(-1.78, 4.94) * mm});
            skLineSegment(sketch, "E368", {"start": v(-1.78, 4.94) * mm, "end": v(-1.77, 4.83) * mm});
            skLineSegment(sketch, "E369", {"start": v(-1.77, 4.83) * mm, "end": v(-1.77, 4.83) * mm});
            skLineSegment(sketch, "E370", {"start": v(-1.77, 4.83) * mm, "end": v(-1.76, 4.8) * mm});
            skLineSegment(sketch, "E371", {"start": v(-1.76, 4.8) * mm, "end": v(-1.76, 4.8) * mm});
            skLineSegment(sketch, "E372", {"start": v(-4.52, 2.78) * mm, "end": v(-4.53, 2.79) * mm});
            skLineSegment(sketch, "E373", {"start": v(-4.53, 2.79) * mm, "end": v(-4.6, 2.88) * mm});
            skLineSegment(sketch, "E374", {"start": v(-4.6, 2.88) * mm, "end": v(-4.6, 2.88) * mm});
            skLineSegment(sketch, "E375", {"start": v(-4.6, 2.88) * mm, "end": v(-4.66, 2.98) * mm});
            skLineSegment(sketch, "E376", {"start": v(-4.66, 2.98) * mm, "end": v(-4.66, 2.98) * mm});
            skLineSegment(sketch, "E377", {"start": v(-4.66, 2.98) * mm, "end": v(-4.7, 3.1) * mm});
            skLineSegment(sketch, "E378", {"start": v(-4.7, 3.1) * mm, "end": v(-4.7, 3.1) * mm});
            skLineSegment(sketch, "E379", {"start": v(-4.7, 3.1) * mm, "end": v(-4.7, 3.12) * mm});
            skLineSegment(sketch, "E380", {"start": v(-4.7, 3.12) * mm, "end": v(-4.7, 3.14) * mm});
            skLineSegment(sketch, "E381", {"start": v(-4.7, 3.14) * mm, "end": v(-4.7, 3.16) * mm});
            skLineSegment(sketch, "E382", {"start": v(-4.7, 3.16) * mm, "end": v(-4.69, 3.17) * mm});
            skLineSegment(sketch, "E383", {"start": v(-4.69, 3.17) * mm, "end": v(-4.68, 3.18) * mm});
            skLineSegment(sketch, "E384", {"start": v(-4.68, 3.18) * mm, "end": v(-4.66, 3.2) * mm});
            skLineSegment(sketch, "E385", {"start": v(-4.66, 3.2) * mm, "end": v(-4.65, 3.2) * mm});
            skLineSegment(sketch, "E386", {"start": v(-4.65, 3.2) * mm, "end": v(-4.64, 3.21) * mm});
            skLineSegment(sketch, "E387", {"start": v(-4.64, 3.21) * mm, "end": v(-4.62, 3.22) * mm});
            skLineSegment(sketch, "E388", {"start": v(-4.62, 3.22) * mm, "end": v(-4.6, 3.22) * mm});
            skLineSegment(sketch, "E389", {"start": v(-4.6, 3.22) * mm, "end": v(-4.59, 3.22) * mm});
            skLineSegment(sketch, "E390", {"start": v(-4.59, 3.22) * mm, "end": v(-4.57, 3.21) * mm});
            skLineSegment(sketch, "E391", {"start": v(-4.57, 3.21) * mm, "end": v(-4.56, 3.2) * mm});
            skLineSegment(sketch, "E392", {"start": v(-4.56, 3.2) * mm, "end": v(-4.54, 3.2) * mm});
            skLineSegment(sketch, "E393", {"start": v(-4.54, 3.2) * mm, "end": v(-4.53, 3.19) * mm});
            skLineSegment(sketch, "E394", {"start": v(-4.53, 3.19) * mm, "end": v(-4.52, 3.17) * mm});
            skLineSegment(sketch, "E395", {"start": v(-4.52, 3.17) * mm, "end": v(-4.51, 3.16) * mm});
            skLineSegment(sketch, "E396", {"start": v(-4.51, 3.16) * mm, "end": v(-4.5, 3.14) * mm});
            skLineSegment(sketch, "E397", {"start": v(-4.5, 3.14) * mm, "end": v(-4.5, 3.14) * mm});
            skLineSegment(sketch, "E398", {"start": v(-4.5, 3.14) * mm, "end": v(-4.48, 3.06) * mm});
            skLineSegment(sketch, "E399", {"start": v(-4.48, 3.06) * mm, "end": v(-4.48, 3.06) * mm});
            skLineSegment(sketch, "E400", {"start": v(-4.48, 3.06) * mm, "end": v(-4.44, 3) * mm});
            skLineSegment(sketch, "E401", {"start": v(-4.44, 3) * mm, "end": v(-4.43, 2.99) * mm});
            skLineSegment(sketch, "E402", {"start": v(-4.43, 2.99) * mm, "end": v(-4.38, 2.93) * mm});
            skLineSegment(sketch, "E403", {"start": v(-4.38, 2.93) * mm, "end": v(-4.38, 2.93) * mm});
            skLineSegment(sketch, "E404", {"start": v(-4.38, 2.93) * mm, "end": v(-4.32, 2.87) * mm});
            skLineSegment(sketch, "E405", {"start": v(-4.32, 2.87) * mm, "end": v(-4.32, 2.87) * mm});
            skLineSegment(sketch, "E406", {"start": v(-4.32, 2.87) * mm, "end": v(-4.25, 2.83) * mm});
            skLineSegment(sketch, "E407", {"start": v(-4.25, 2.83) * mm, "end": v(-4.25, 2.83) * mm});
            skLineSegment(sketch, "E408", {"start": v(-4.25, 2.83) * mm, "end": v(-4.17, 2.8) * mm});
            skLineSegment(sketch, "E409", {"start": v(-4.17, 2.8) * mm, "end": v(-4.17, 2.8) * mm});
            skLineSegment(sketch, "E410", {"start": v(-4.17, 2.8) * mm, "end": v(-4.1, 2.78) * mm});
            skLineSegment(sketch, "E411", {"start": v(-4.1, 2.78) * mm, "end": v(-4.1, 2.78) * mm});
            skLineSegment(sketch, "E412", {"start": v(-4.1, 2.78) * mm, "end": v(-4.01, 2.77) * mm});
            skLineSegment(sketch, "E413", {"start": v(-4.01, 2.77) * mm, "end": v(-4, 2.77) * mm});
            skLineSegment(sketch, "E414", {"start": v(-4, 2.77) * mm, "end": v(-3.93, 2.78) * mm});
            skLineSegment(sketch, "E415", {"start": v(-3.93, 2.78) * mm, "end": v(-3.92, 2.78) * mm});
            skLineSegment(sketch, "E416", {"start": v(-3.92, 2.78) * mm, "end": v(-3.85, 2.8) * mm});
            skLineSegment(sketch, "E417", {"start": v(-3.85, 2.8) * mm, "end": v(-3.84, 2.8) * mm});
            skLineSegment(sketch, "E418", {"start": v(-3.84, 2.8) * mm, "end": v(-3.77, 2.84) * mm});
            skLineSegment(sketch, "E419", {"start": v(-3.77, 2.84) * mm, "end": v(-3.77, 2.84) * mm});
            skLineSegment(sketch, "E420", {"start": v(-3.77, 2.84) * mm, "end": v(-3.7, 2.89) * mm});
            skLineSegment(sketch, "E421", {"start": v(-3.7, 2.89) * mm, "end": v(-3.7, 2.89) * mm});
            skLineSegment(sketch, "E422", {"start": v(-3.7, 2.89) * mm, "end": v(-3.64, 2.94) * mm});
            skLineSegment(sketch, "E423", {"start": v(-3.64, 2.94) * mm, "end": v(-3.64, 2.95) * mm});
            skLineSegment(sketch, "E424", {"start": v(-3.64, 2.95) * mm, "end": v(-3.6, 3.01) * mm});
            skLineSegment(sketch, "E425", {"start": v(-3.6, 3.01) * mm, "end": v(-3.6, 3.01) * mm});
            skLineSegment(sketch, "E426", {"start": v(-3.6, 3.01) * mm, "end": v(-3.56, 3.09) * mm});
            skLineSegment(sketch, "E427", {"start": v(-3.56, 3.09) * mm, "end": v(-3.56, 3.09) * mm});
            skLineSegment(sketch, "E428", {"start": v(-3.56, 3.09) * mm, "end": v(-3.53, 3.17) * mm});
            skLineSegment(sketch, "E429", {"start": v(-4.5, 2.76) * mm, "end": v(-4.52, 2.78) * mm});
            skLineSegment(sketch, "E430", {"start": v(-3.78, 3.73) * mm, "end": v(-3.78, 3.73) * mm});
            skLineSegment(sketch, "E431", {"start": v(-3.78, 3.73) * mm, "end": v(-3.86, 3.76) * mm});
            skLineSegment(sketch, "E432", {"start": v(-3.86, 3.76) * mm, "end": v(-3.87, 3.77) * mm});
            skLineSegment(sketch, "E433", {"start": v(-3.87, 3.77) * mm, "end": v(-3.89, 3.78) * mm});
            skLineSegment(sketch, "E434", {"start": v(-3.89, 3.78) * mm, "end": v(-3.9, 3.79) * mm});
            skLineSegment(sketch, "E435", {"start": v(-3.9, 3.79) * mm, "end": v(-3.91, 3.8) * mm});
            skLineSegment(sketch, "E436", {"start": v(-3.91, 3.8) * mm, "end": v(-3.92, 3.81) * mm});
            skLineSegment(sketch, "E437", {"start": v(-3.92, 3.81) * mm, "end": v(-3.93, 3.83) * mm});
            skLineSegment(sketch, "E438", {"start": v(-3.93, 3.83) * mm, "end": v(-3.93, 3.84) * mm});
            skLineSegment(sketch, "E439", {"start": v(-3.93, 3.84) * mm, "end": v(-3.93, 3.86) * mm});
            skLineSegment(sketch, "E440", {"start": v(-3.93, 3.86) * mm, "end": v(-3.93, 3.88) * mm});
            skLineSegment(sketch, "E441", {"start": v(-3.75, 3.7) * mm, "end": v(-3.75, 3.71) * mm});
            skLineSegment(sketch, "E442", {"start": v(-3.75, 3.71) * mm, "end": v(-3.76, 3.72) * mm});
            skLineSegment(sketch, "E443", {"start": v(-3.76, 3.72) * mm, "end": v(-3.77, 3.72) * mm});
            skLineSegment(sketch, "E444", {"start": v(-3.77, 3.72) * mm, "end": v(-3.78, 3.73) * mm});
            skLineSegment(sketch, "E445", {"start": v(-3.93, 3.88) * mm, "end": v(-3.93, 3.89) * mm});
            skLineSegment(sketch, "E446", {"start": v(-3.93, 3.89) * mm, "end": v(-3.93, 3.9) * mm});
            skLineSegment(sketch, "E447", {"start": v(-3.93, 3.9) * mm, "end": v(-3.92, 3.91) * mm});
            skLineSegment(sketch, "E448", {"start": v(-3.92, 3.91) * mm, "end": v(-3.91, 3.93) * mm});
            skLineSegment(sketch, "E449", {"start": v(-3.91, 3.93) * mm, "end": v(-3.9, 3.96) * mm});
            skLineSegment(sketch, "E450", {"start": v(-1.76, 4.8) * mm, "end": v(-1.75, 4.77) * mm});
            skSolve(sketch);
        }
        {
            var Q0;
            Q0=makeQuery(id+"F0.imprint","IMPRINT",FACE,{"disambiguationData":[TD([[makeQuery(id+"F0.imprint","IMPRINT",EDGE,{"derivedFrom":sQuery(id+"F0.wireOp",EDGE,"E0")}),-1.0]])]});
            extrude(context, id + "F1", {"entities" : qUnion([Q0]), "depth" : 1 * mm});
        }
        {
            var Q0;
            Q0=makeQuery(id+"F1.opExtrude","CAP_FACE",FACE,{"disambiguationData":[OSD([sQuery(id+"F0.wireOp",EDGE,"E0"),sQuery(id+"F0.wireOp",EDGE,"E1"),sQuery(id+"F0.wireOp",EDGE,"E2"),sQuery(id+"F0.wireOp",EDGE,"E3"),sQuery(id+"F0.wireOp",EDGE,"E4"),sQuery(id+"F0.wireOp",EDGE,"E5"),sQuery(id+"F0.wireOp",EDGE,"E6"),sQuery(id+"F0.wireOp",EDGE,"E7"),sQuery(id+"F0.wireOp",EDGE,"E8"),sQuery(id+"F0.wireOp",EDGE,"E9"),sQuery(id+"F0.wireOp",EDGE,"E10"),sQuery(id+"F0.wireOp",EDGE,"E11"),sQuery(id+"F0.wireOp",EDGE,"E12"),sQuery(id+"F0.wireOp",EDGE,"E13"),sQuery(id+"F0.wireOp",EDGE,"E14"),sQuery(id+"F0.wireOp",EDGE,"E15"),sQuery(id+"F0.wireOp",EDGE,"E16"),sQuery(id+"F0.wireOp",EDGE,"E17"),sQuery(id+"F0.wireOp",EDGE,"E18"),sQuery(id+"F0.wireOp",EDGE,"E19"),sQuery(id+"F0.wireOp",EDGE,"E20"),sQuery(id+"F0.wireOp",EDGE,"E21"),sQuery(id+"F0.wireOp",EDGE,"E22"),sQuery(id+"F0.wireOp",EDGE,"E23"),sQuery(id+"F0.wireOp",EDGE,"E24"),sQuery(id+"F0.wireOp",EDGE,"E25"),sQuery(id+"F0.wireOp",EDGE,"E26"),sQuery(id+"F0.wireOp",EDGE,"E27"),sQuery(id+"F0.wireOp",EDGE,"E28"),sQuery(id+"F0.wireOp",EDGE,"E29"),sQuery(id+"F0.wireOp",EDGE,"E30"),sQuery(id+"F0.wireOp",EDGE,"E31"),sQuery(id+"F0.wireOp",EDGE,"E32"),sQuery(id+"F0.wireOp",EDGE,"E33"),sQuery(id+"F0.wireOp",EDGE,"E34"),sQuery(id+"F0.wireOp",EDGE,"E35"),sQuery(id+"F0.wireOp",EDGE,"E36"),sQuery(id+"F0.wireOp",EDGE,"E37"),sQuery(id+"F0.wireOp",EDGE,"E38"),sQuery(id+"F0.wireOp",EDGE,"E39"),sQuery(id+"F0.wireOp",EDGE,"E40"),sQuery(id+"F0.wireOp",EDGE,"E41"),sQuery(id+"F0.wireOp",EDGE,"E42"),sQuery(id+"F0.wireOp",EDGE,"E43"),sQuery(id+"F0.wireOp",EDGE,"E44"),sQuery(id+"F0.wireOp",EDGE,"E45"),sQuery(id+"F0.wireOp",EDGE,"E46"),sQuery(id+"F0.wireOp",EDGE,"E47"),sQuery(id+"F0.wireOp",EDGE,"E48"),sQuery(id+"F0.wireOp",EDGE,"E49"),sQuery(id+"F0.wireOp",EDGE,"E50"),sQuery(id+"F0.wireOp",EDGE,"E51"),sQuery(id+"F0.wireOp",EDGE,"E52"),sQuery(id+"F0.wireOp",EDGE,"E53"),sQuery(id+"F0.wireOp",EDGE,"E54"),sQuery(id+"F0.wireOp",EDGE,"E55"),sQuery(id+"F0.wireOp",EDGE,"E56"),sQuery(id+"F0.wireOp",EDGE,"E57"),sQuery(id+"F0.wireOp",EDGE,"E58"),sQuery(id+"F0.wireOp",EDGE,"E59"),sQuery(id+"F0.wireOp",EDGE,"E60"),sQuery(id+"F0.wireOp",EDGE,"E61"),sQuery(id+"F0.wireOp",EDGE,"E62"),sQuery(id+"F0.wireOp",EDGE,"E63"),sQuery(id+"F0.wireOp",EDGE,"E64"),sQuery(id+"F0.wireOp",EDGE,"E65"),sQuery(id+"F0.wireOp",EDGE,"E66"),sQuery(id+"F0.wireOp",EDGE,"E67"),sQuery(id+"F0.wireOp",EDGE,"E68"),sQuery(id+"F0.wireOp",EDGE,"E69"),sQuery(id+"F0.wireOp",EDGE,"E70"),sQuery(id+"F0.wireOp",EDGE,"E71"),sQuery(id+"F0.wireOp",EDGE,"E72"),sQuery(id+"F0.wireOp",EDGE,"E73"),sQuery(id+"F0.wireOp",EDGE,"E74"),sQuery(id+"F0.wireOp",EDGE,"E75"),sQuery(id+"F0.wireOp",EDGE,"E76"),sQuery(id+"F0.wireOp",EDGE,"E77"),sQuery(id+"F0.wireOp",EDGE,"E78"),sQuery(id+"F0.wireOp",EDGE,"E79"),sQuery(id+"F0.wireOp",EDGE,"E80"),sQuery(id+"F0.wireOp",EDGE,"E81"),sQuery(id+"F0.wireOp",EDGE,"E82"),sQuery(id+"F0.wireOp",EDGE,"E83"),sQuery(id+"F0.wireOp",EDGE,"E84"),sQuery(id+"F0.wireOp",EDGE,"E85"),sQuery(id+"F0.wireOp",EDGE,"E86"),sQuery(id+"F0.wireOp",EDGE,"E87"),sQuery(id+"F0.wireOp",EDGE,"E88"),sQuery(id+"F0.wireOp",EDGE,"E89"),sQuery(id+"F0.wireOp",EDGE,"E90"),sQuery(id+"F0.wireOp",EDGE,"E91"),sQuery(id+"F0.wireOp",EDGE,"E92"),sQuery(id+"F0.wireOp",EDGE,"E93"),sQuery(id+"F0.wireOp",EDGE,"E94"),sQuery(id+"F0.wireOp",EDGE,"E95"),sQuery(id+"F0.wireOp",EDGE,"E96"),sQuery(id+"F0.wireOp",EDGE,"E97"),sQuery(id+"F0.wireOp",EDGE,"E98"),sQuery(id+"F0.wireOp",EDGE,"E99"),sQuery(id+"F0.wireOp",EDGE,"E100"),sQuery(id+"F0.wireOp",EDGE,"E101"),sQuery(id+"F0.wireOp",EDGE,"E102"),sQuery(id+"F0.wireOp",EDGE,"E103"),sQuery(id+"F0.wireOp",EDGE,"E104"),sQuery(id+"F0.wireOp",EDGE,"E105"),sQuery(id+"F0.wireOp",EDGE,"E106"),sQuery(id+"F0.wireOp",EDGE,"E107"),sQuery(id+"F0.wireOp",EDGE,"E108"),sQuery(id+"F0.wireOp",EDGE,"E109"),sQuery(id+"F0.wireOp",EDGE,"E110"),sQuery(id+"F0.wireOp",EDGE,"E111"),sQuery(id+"F0.wireOp",EDGE,"E112"),sQuery(id+"F0.wireOp",EDGE,"E113"),sQuery(id+"F0.wireOp",EDGE,"E114"),sQuery(id+"F0.wireOp",EDGE,"E115"),sQuery(id+"F0.wireOp",EDGE,"E116"),sQuery(id+"F0.wireOp",EDGE,"E117"),sQuery(id+"F0.wireOp",EDGE,"E118"),sQuery(id+"F0.wireOp",EDGE,"E119"),sQuery(id+"F0.wireOp",EDGE,"E120"),sQuery(id+"F0.wireOp",EDGE,"E121"),sQuery(id+"F0.wireOp",EDGE,"E122"),sQuery(id+"F0.wireOp",EDGE,"E123"),sQuery(id+"F0.wireOp",EDGE,"E124"),sQuery(id+"F0.wireOp",EDGE,"E125"),sQuery(id+"F0.wireOp",EDGE,"E126"),sQuery(id+"F0.wireOp",EDGE,"E127"),sQuery(id+"F0.wireOp",EDGE,"E128"),sQuery(id+"F0.wireOp",EDGE,"E129"),sQuery(id+"F0.wireOp",EDGE,"E130"),sQuery(id+"F0.wireOp",EDGE,"E131"),sQuery(id+"F0.wireOp",EDGE,"E132"),sQuery(id+"F0.wireOp",EDGE,"E133"),sQuery(id+"F0.wireOp",EDGE,"E134"),sQuery(id+"F0.wireOp",EDGE,"E135"),sQuery(id+"F0.wireOp",EDGE,"E136"),sQuery(id+"F0.wireOp",EDGE,"E137"),sQuery(id+"F0.wireOp",EDGE,"E138"),sQuery(id+"F0.wireOp",EDGE,"E139"),sQuery(id+"F0.wireOp",EDGE,"E140"),sQuery(id+"F0.wireOp",EDGE,"E141"),sQuery(id+"F0.wireOp",EDGE,"E142"),sQuery(id+"F0.wireOp",EDGE,"E143"),sQuery(id+"F0.wireOp",EDGE,"E144"),sQuery(id+"F0.wireOp",EDGE,"E145"),sQuery(id+"F0.wireOp",EDGE,"E146"),sQuery(id+"F0.wireOp",EDGE,"E147"),sQuery(id+"F0.wireOp",EDGE,"E148"),sQuery(id+"F0.wireOp",EDGE,"E149"),sQuery(id+"F0.wireOp",EDGE,"E150"),sQuery(id+"F0.wireOp",EDGE,"E151"),sQuery(id+"F0.wireOp",EDGE,"E152"),sQuery(id+"F0.wireOp",EDGE,"E153"),sQuery(id+"F0.wireOp",EDGE,"E154"),sQuery(id+"F0.wireOp",EDGE,"E155"),sQuery(id+"F0.wireOp",EDGE,"E156"),sQuery(id+"F0.wireOp",EDGE,"E157"),sQuery(id+"F0.wireOp",EDGE,"E158"),sQuery(id+"F0.wireOp",EDGE,"E159"),sQuery(id+"F0.wireOp",EDGE,"E160"),sQuery(id+"F0.wireOp",EDGE,"E161"),sQuery(id+"F0.wireOp",EDGE,"E162"),sQuery(id+"F0.wireOp",EDGE,"E163"),sQuery(id+"F0.wireOp",EDGE,"E164"),sQuery(id+"F0.wireOp",EDGE,"E165"),sQuery(id+"F0.wireOp",EDGE,"E166"),sQuery(id+"F0.wireOp",EDGE,"E167"),sQuery(id+"F0.wireOp",EDGE,"E168"),sQuery(id+"F0.wireOp",EDGE,"E169"),sQuery(id+"F0.wireOp",EDGE,"E170"),sQuery(id+"F0.wireOp",EDGE,"E171"),sQuery(id+"F0.wireOp",EDGE,"E172"),sQuery(id+"F0.wireOp",EDGE,"E173"),sQuery(id+"F0.wireOp",EDGE,"E174"),sQuery(id+"F0.wireOp",EDGE,"E175"),sQuery(id+"F0.wireOp",EDGE,"E176"),sQuery(id+"F0.wireOp",EDGE,"E177"),sQuery(id+"F0.wireOp",EDGE,"E178"),sQuery(id+"F0.wireOp",EDGE,"E179"),sQuery(id+"F0.wireOp",EDGE,"E180"),sQuery(id+"F0.wireOp",EDGE,"E181"),sQuery(id+"F0.wireOp",EDGE,"E182"),sQuery(id+"F0.wireOp",EDGE,"E183"),sQuery(id+"F0.wireOp",EDGE,"E184"),sQuery(id+"F0.wireOp",EDGE,"E185"),sQuery(id+"F0.wireOp",EDGE,"E186"),sQuery(id+"F0.wireOp",EDGE,"E187"),sQuery(id+"F0.wireOp",EDGE,"E188"),sQuery(id+"F0.wireOp",EDGE,"E189"),sQuery(id+"F0.wireOp",EDGE,"E190"),sQuery(id+"F0.wireOp",EDGE,"E191"),sQuery(id+"F0.wireOp",EDGE,"E192"),sQuery(id+"F0.wireOp",EDGE,"E193"),sQuery(id+"F0.wireOp",EDGE,"E194"),sQuery(id+"F0.wireOp",EDGE,"E195"),sQuery(id+"F0.wireOp",EDGE,"E196"),sQuery(id+"F0.wireOp",EDGE,"E197"),sQuery(id+"F0.wireOp",EDGE,"E198"),sQuery(id+"F0.wireOp",EDGE,"E199"),sQuery(id+"F0.wireOp",EDGE,"E200"),sQuery(id+"F0.wireOp",EDGE,"E201"),sQuery(id+"F0.wireOp",EDGE,"E202"),sQuery(id+"F0.wireOp",EDGE,"E203"),sQuery(id+"F0.wireOp",EDGE,"E204"),sQuery(id+"F0.wireOp",EDGE,"E205"),sQuery(id+"F0.wireOp",EDGE,"E206"),sQuery(id+"F0.wireOp",EDGE,"E207"),sQuery(id+"F0.wireOp",EDGE,"E208"),sQuery(id+"F0.wireOp",EDGE,"E209"),sQuery(id+"F0.wireOp",EDGE,"E210"),sQuery(id+"F0.wireOp",EDGE,"E211"),sQuery(id+"F0.wireOp",EDGE,"E212"),sQuery(id+"F0.wireOp",EDGE,"E213"),sQuery(id+"F0.wireOp",EDGE,"E214"),sQuery(id+"F0.wireOp",EDGE,"E215"),sQuery(id+"F0.wireOp",EDGE,"E216"),sQuery(id+"F0.wireOp",EDGE,"E217"),sQuery(id+"F0.wireOp",EDGE,"E218"),sQuery(id+"F0.wireOp",EDGE,"E219"),sQuery(id+"F0.wireOp",EDGE,"E220"),sQuery(id+"F0.wireOp",EDGE,"E221"),sQuery(id+"F0.wireOp",EDGE,"E222"),sQuery(id+"F0.wireOp",EDGE,"E223"),sQuery(id+"F0.wireOp",EDGE,"E224"),sQuery(id+"F0.wireOp",EDGE,"E225"),sQuery(id+"F0.wireOp",EDGE,"E226"),sQuery(id+"F0.wireOp",EDGE,"E227"),sQuery(id+"F0.wireOp",EDGE,"E228"),sQuery(id+"F0.wireOp",EDGE,"E229"),sQuery(id+"F0.wireOp",EDGE,"E230"),sQuery(id+"F0.wireOp",EDGE,"E231"),sQuery(id+"F0.wireOp",EDGE,"E232"),sQuery(id+"F0.wireOp",EDGE,"E233"),sQuery(id+"F0.wireOp",EDGE,"E234"),sQuery(id+"F0.wireOp",EDGE,"E235"),sQuery(id+"F0.wireOp",EDGE,"E236"),sQuery(id+"F0.wireOp",EDGE,"E237"),sQuery(id+"F0.wireOp",EDGE,"E238"),sQuery(id+"F0.wireOp",EDGE,"E239"),sQuery(id+"F0.wireOp",EDGE,"E240"),sQuery(id+"F0.wireOp",EDGE,"E241"),sQuery(id+"F0.wireOp",EDGE,"E242"),sQuery(id+"F0.wireOp",EDGE,"E243"),sQuery(id+"F0.wireOp",EDGE,"E244"),sQuery(id+"F0.wireOp",EDGE,"E245"),sQuery(id+"F0.wireOp",EDGE,"E246"),sQuery(id+"F0.wireOp",EDGE,"E247"),sQuery(id+"F0.wireOp",EDGE,"E248"),sQuery(id+"F0.wireOp",EDGE,"E249"),sQuery(id+"F0.wireOp",EDGE,"E250"),sQuery(id+"F0.wireOp",EDGE,"E251"),sQuery(id+"F0.wireOp",EDGE,"E252"),sQuery(id+"F0.wireOp",EDGE,"E253"),sQuery(id+"F0.wireOp",EDGE,"E254"),sQuery(id+"F0.wireOp",EDGE,"E255"),sQuery(id+"F0.wireOp",EDGE,"E256"),sQuery(id+"F0.wireOp",EDGE,"E257"),sQuery(id+"F0.wireOp",EDGE,"E258"),sQuery(id+"F0.wireOp",EDGE,"E259"),sQuery(id+"F0.wireOp",EDGE,"E260"),sQuery(id+"F0.wireOp",EDGE,"E261"),sQuery(id+"F0.wireOp",EDGE,"E262"),sQuery(id+"F0.wireOp",EDGE,"E263"),sQuery(id+"F0.wireOp",EDGE,"E264"),sQuery(id+"F0.wireOp",EDGE,"E265"),sQuery(id+"F0.wireOp",EDGE,"E266"),sQuery(id+"F0.wireOp",EDGE,"E267"),sQuery(id+"F0.wireOp",EDGE,"E268"),sQuery(id+"F0.wireOp",EDGE,"E269"),sQuery(id+"F0.wireOp",EDGE,"E270"),sQuery(id+"F0.wireOp",EDGE,"E271"),sQuery(id+"F0.wireOp",EDGE,"E272"),sQuery(id+"F0.wireOp",EDGE,"E273"),sQuery(id+"F0.wireOp",EDGE,"E274"),sQuery(id+"F0.wireOp",EDGE,"E275"),sQuery(id+"F0.wireOp",EDGE,"E276"),sQuery(id+"F0.wireOp",EDGE,"E277"),sQuery(id+"F0.wireOp",EDGE,"E278"),sQuery(id+"F0.wireOp",EDGE,"E279"),sQuery(id+"F0.wireOp",EDGE,"E280"),sQuery(id+"F0.wireOp",EDGE,"E281"),sQuery(id+"F0.wireOp",EDGE,"E282"),sQuery(id+"F0.wireOp",EDGE,"E283"),sQuery(id+"F0.wireOp",EDGE,"E284"),sQuery(id+"F0.wireOp",EDGE,"E285"),sQuery(id+"F0.wireOp",EDGE,"E286"),sQuery(id+"F0.wireOp",EDGE,"E287"),sQuery(id+"F0.wireOp",EDGE,"E288"),sQuery(id+"F0.wireOp",EDGE,"E289"),sQuery(id+"F0.wireOp",EDGE,"E290"),sQuery(id+"F0.wireOp",EDGE,"E291"),sQuery(id+"F0.wireOp",EDGE,"E292"),sQuery(id+"F0.wireOp",EDGE,"E293"),sQuery(id+"F0.wireOp",EDGE,"E294"),sQuery(id+"F0.wireOp",EDGE,"E295"),sQuery(id+"F0.wireOp",EDGE,"E296"),sQuery(id+"F0.wireOp",EDGE,"E297"),sQuery(id+"F0.wireOp",EDGE,"E298"),sQuery(id+"F0.wireOp",EDGE,"E299"),sQuery(id+"F0.wireOp",EDGE,"E300"),sQuery(id+"F0.wireOp",EDGE,"E301"),sQuery(id+"F0.wireOp",EDGE,"E302"),sQuery(id+"F0.wireOp",EDGE,"E303"),sQuery(id+"F0.wireOp",EDGE,"E304"),sQuery(id+"F0.wireOp",EDGE,"E305"),sQuery(id+"F0.wireOp",EDGE,"E306"),sQuery(id+"F0.wireOp",EDGE,"E307"),sQuery(id+"F0.wireOp",EDGE,"E308"),sQuery(id+"F0.wireOp",EDGE,"E309"),sQuery(id+"F0.wireOp",EDGE,"E310"),sQuery(id+"F0.wireOp",EDGE,"E311"),sQuery(id+"F0.wireOp",EDGE,"E312"),sQuery(id+"F0.wireOp",EDGE,"E313"),sQuery(id+"F0.wireOp",EDGE,"E314"),sQuery(id+"F0.wireOp",EDGE,"E315"),sQuery(id+"F0.wireOp",EDGE,"E316"),sQuery(id+"F0.wireOp",EDGE,"E317"),sQuery(id+"F0.wireOp",EDGE,"E318"),sQuery(id+"F0.wireOp",EDGE,"E319"),sQuery(id+"F0.wireOp",EDGE,"E320"),sQuery(id+"F0.wireOp",EDGE,"E321"),sQuery(id+"F0.wireOp",EDGE,"E322"),sQuery(id+"F0.wireOp",EDGE,"E323"),sQuery(id+"F0.wireOp",EDGE,"E324"),sQuery(id+"F0.wireOp",EDGE,"E325"),sQuery(id+"F0.wireOp",EDGE,"E326"),sQuery(id+"F0.wireOp",EDGE,"E327"),sQuery(id+"F0.wireOp",EDGE,"E328"),sQuery(id+"F0.wireOp",EDGE,"E329"),sQuery(id+"F0.wireOp",EDGE,"E330"),sQuery(id+"F0.wireOp",EDGE,"E331"),sQuery(id+"F0.wireOp",EDGE,"E332"),sQuery(id+"F0.wireOp",EDGE,"E333"),sQuery(id+"F0.wireOp",EDGE,"E334"),sQuery(id+"F0.wireOp",EDGE,"E335"),sQuery(id+"F0.wireOp",EDGE,"E336"),sQuery(id+"F0.wireOp",EDGE,"E337"),sQuery(id+"F0.wireOp",EDGE,"E338"),sQuery(id+"F0.wireOp",EDGE,"E339"),sQuery(id+"F0.wireOp",EDGE,"E340"),sQuery(id+"F0.wireOp",EDGE,"E341"),sQuery(id+"F0.wireOp",EDGE,"E342"),sQuery(id+"F0.wireOp",EDGE,"E343"),sQuery(id+"F0.wireOp",EDGE,"E344"),sQuery(id+"F0.wireOp",EDGE,"E345"),sQuery(id+"F0.wireOp",EDGE,"E346"),sQuery(id+"F0.wireOp",EDGE,"E347"),sQuery(id+"F0.wireOp",EDGE,"E348"),sQuery(id+"F0.wireOp",EDGE,"E349"),sQuery(id+"F0.wireOp",EDGE,"E350"),sQuery(id+"F0.wireOp",EDGE,"E351"),sQuery(id+"F0.wireOp",EDGE,"E352"),sQuery(id+"F0.wireOp",EDGE,"E353"),sQuery(id+"F0.wireOp",EDGE,"E354"),sQuery(id+"F0.wireOp",EDGE,"E355"),sQuery(id+"F0.wireOp",EDGE,"E356"),sQuery(id+"F0.wireOp",EDGE,"E357"),sQuery(id+"F0.wireOp",EDGE,"E358"),sQuery(id+"F0.wireOp",EDGE,"E359"),sQuery(id+"F0.wireOp",EDGE,"E360"),sQuery(id+"F0.wireOp",EDGE,"E361"),sQuery(id+"F0.wireOp",EDGE,"E362"),sQuery(id+"F0.wireOp",EDGE,"E363"),sQuery(id+"F0.wireOp",EDGE,"E364"),sQuery(id+"F0.wireOp",EDGE,"E365"),sQuery(id+"F0.wireOp",EDGE,"E366"),sQuery(id+"F0.wireOp",EDGE,"E367"),sQuery(id+"F0.wireOp",EDGE,"E368"),sQuery(id+"F0.wireOp",EDGE,"E369"),sQuery(id+"F0.wireOp",EDGE,"E370"),sQuery(id+"F0.wireOp",EDGE,"E371"),sQuery(id+"F0.wireOp",EDGE,"E372"),sQuery(id+"F0.wireOp",EDGE,"E373"),sQuery(id+"F0.wireOp",EDGE,"E374"),sQuery(id+"F0.wireOp",EDGE,"E375"),sQuery(id+"F0.wireOp",EDGE,"E376"),sQuery(id+"F0.wireOp",EDGE,"E377"),sQuery(id+"F0.wireOp",EDGE,"E378"),sQuery(id+"F0.wireOp",EDGE,"E379"),sQuery(id+"F0.wireOp",EDGE,"E380"),sQuery(id+"F0.wireOp",EDGE,"E381"),sQuery(id+"F0.wireOp",EDGE,"E382"),sQuery(id+"F0.wireOp",EDGE,"E383"),sQuery(id+"F0.wireOp",EDGE,"E384"),sQuery(id+"F0.wireOp",EDGE,"E385"),sQuery(id+"F0.wireOp",EDGE,"E386"),sQuery(id+"F0.wireOp",EDGE,"E387"),sQuery(id+"F0.wireOp",EDGE,"E388"),sQuery(id+"F0.wireOp",EDGE,"E389"),sQuery(id+"F0.wireOp",EDGE,"E390"),sQuery(id+"F0.wireOp",EDGE,"E391"),sQuery(id+"F0.wireOp",EDGE,"E392"),sQuery(id+"F0.wireOp",EDGE,"E393"),sQuery(id+"F0.wireOp",EDGE,"E394"),sQuery(id+"F0.wireOp",EDGE,"E395"),sQuery(id+"F0.wireOp",EDGE,"E396"),sQuery(id+"F0.wireOp",EDGE,"E397"),sQuery(id+"F0.wireOp",EDGE,"E398"),sQuery(id+"F0.wireOp",EDGE,"E399"),sQuery(id+"F0.wireOp",EDGE,"E400"),sQuery(id+"F0.wireOp",EDGE,"E401"),sQuery(id+"F0.wireOp",EDGE,"E402"),sQuery(id+"F0.wireOp",EDGE,"E403"),sQuery(id+"F0.wireOp",EDGE,"E404"),sQuery(id+"F0.wireOp",EDGE,"E405"),sQuery(id+"F0.wireOp",EDGE,"E406"),sQuery(id+"F0.wireOp",EDGE,"E407"),sQuery(id+"F0.wireOp",EDGE,"E408"),sQuery(id+"F0.wireOp",EDGE,"E409"),sQuery(id+"F0.wireOp",EDGE,"E410"),sQuery(id+"F0.wireOp",EDGE,"E411"),sQuery(id+"F0.wireOp",EDGE,"E412"),sQuery(id+"F0.wireOp",EDGE,"E413"),sQuery(id+"F0.wireOp",EDGE,"E414"),sQuery(id+"F0.wireOp",EDGE,"E415"),sQuery(id+"F0.wireOp",EDGE,"E416"),sQuery(id+"F0.wireOp",EDGE,"E417"),sQuery(id+"F0.wireOp",EDGE,"E418"),sQuery(id+"F0.wireOp",EDGE,"E419"),sQuery(id+"F0.wireOp",EDGE,"E420"),sQuery(id+"F0.wireOp",EDGE,"E421"),sQuery(id+"F0.wireOp",EDGE,"E422"),sQuery(id+"F0.wireOp",EDGE,"E423"),sQuery(id+"F0.wireOp",EDGE,"E424"),sQuery(id+"F0.wireOp",EDGE,"E425"),sQuery(id+"F0.wireOp",EDGE,"E426"),sQuery(id+"F0.wireOp",EDGE,"E427"),sQuery(id+"F0.wireOp",EDGE,"E428"),sQuery(id+"F0.wireOp",EDGE,"E429"),sQuery(id+"F0.wireOp",EDGE,"E430"),sQuery(id+"F0.wireOp",EDGE,"E431"),sQuery(id+"F0.wireOp",EDGE,"E432"),sQuery(id+"F0.wireOp",EDGE,"E433"),sQuery(id+"F0.wireOp",EDGE,"E434"),sQuery(id+"F0.wireOp",EDGE,"E435"),sQuery(id+"F0.wireOp",EDGE,"E436"),sQuery(id+"F0.wireOp",EDGE,"E437"),sQuery(id+"F0.wireOp",EDGE,"E438"),sQuery(id+"F0.wireOp",EDGE,"E439"),sQuery(id+"F0.wireOp",EDGE,"E440"),sQuery(id+"F0.wireOp",EDGE,"E441"),sQuery(id+"F0.wireOp",EDGE,"E442"),sQuery(id+"F0.wireOp",EDGE,"E443"),sQuery(id+"F0.wireOp",EDGE,"E444"),sQuery(id+"F0.wireOp",EDGE,"E445"),sQuery(id+"F0.wireOp",EDGE,"E446"),sQuery(id+"F0.wireOp",EDGE,"E447"),sQuery(id+"F0.wireOp",EDGE,"E448"),sQuery(id+"F0.wireOp",EDGE,"E449"),sQuery(id+"F0.wireOp",EDGE,"E450")])],"isStart":false});
            var sketch = newSketch(context, id + "F2", { "sketchPlane" : qUnion([Q0])});
            skCircle(sketch, "E451", {"center": v(-1.9, 2.5) * mm, "radius": 1.2 * mm});
            skCircle(sketch, "E452", {"center": v(0, 0.7) * mm, "radius": 1.1 * mm});
            skSolve(sketch);
        }
        {
            var Q0;
            Q0=makeQuery(id+"F2.imprint","IMPRINT",FACE,{"disambiguationData":[TD([[makeQuery(id+"F2.imprint","IMPRINT",EDGE,{"derivedFrom":sQuery(id+"F2.wireOp",EDGE,"E452")}),1.0]])]});
            var Q1;
            Q1=makeQuery(id+"F2.imprint","IMPRINT",FACE,{"disambiguationData":[TD([[makeQuery(id+"F2.imprint","IMPRINT",EDGE,{"derivedFrom":sQuery(id+"F2.wireOp",EDGE,"E451")}),1.0]])]});
            var Q2;
            Q2=sQuery(id+"F2.wireOp",EDGE,"E451");
            var Q3;
            Q3=sQuery(id+"F2.wireOp",EDGE,"E452");
            extrude(context, id + "F3", {"entities" : qUnion([Q0, Q1]), "operationType" : NewBodyOperationType.REMOVE, "surfaceEntities" : qUnion([Q2, Q3]), "oppositeDirection" : true, "depth" : 2 * mm});
        }
        {
            var Q0;
            Q0=makeQuery(id+"F1.opExtrude","SWEPT_BODY",BODY,{"disambiguationData":[OSD([sQuery(id+"F0.wireOp",EDGE,"E0"),sQuery(id+"F0.wireOp",EDGE,"E1"),sQuery(id+"F0.wireOp",EDGE,"E2"),sQuery(id+"F0.wireOp",EDGE,"E3"),sQuery(id+"F0.wireOp",EDGE,"E4"),sQuery(id+"F0.wireOp",EDGE,"E5"),sQuery(id+"F0.wireOp",EDGE,"E6"),sQuery(id+"F0.wireOp",EDGE,"E7"),sQuery(id+"F0.wireOp",EDGE,"E8"),sQuery(id+"F0.wireOp",EDGE,"E9"),sQuery(id+"F0.wireOp",EDGE,"E10"),sQuery(id+"F0.wireOp",EDGE,"E11"),sQuery(id+"F0.wireOp",EDGE,"E12"),sQuery(id+"F0.wireOp",EDGE,"E13"),sQuery(id+"F0.wireOp",EDGE,"E14"),sQuery(id+"F0.wireOp",EDGE,"E15"),sQuery(id+"F0.wireOp",EDGE,"E16"),sQuery(id+"F0.wireOp",EDGE,"E17"),sQuery(id+"F0.wireOp",EDGE,"E18"),sQuery(id+"F0.wireOp",EDGE,"E19"),sQuery(id+"F0.wireOp",EDGE,"E20"),sQuery(id+"F0.wireOp",EDGE,"E21"),sQuery(id+"F0.wireOp",EDGE,"E22"),sQuery(id+"F0.wireOp",EDGE,"E23"),sQuery(id+"F0.wireOp",EDGE,"E24"),sQuery(id+"F0.wireOp",EDGE,"E25"),sQuery(id+"F0.wireOp",EDGE,"E26"),sQuery(id+"F0.wireOp",EDGE,"E27"),sQuery(id+"F0.wireOp",EDGE,"E28"),sQuery(id+"F0.wireOp",EDGE,"E29"),sQuery(id+"F0.wireOp",EDGE,"E30"),sQuery(id+"F0.wireOp",EDGE,"E31"),sQuery(id+"F0.wireOp",EDGE,"E32"),sQuery(id+"F0.wireOp",EDGE,"E33"),sQuery(id+"F0.wireOp",EDGE,"E34"),sQuery(id+"F0.wireOp",EDGE,"E35"),sQuery(id+"F0.wireOp",EDGE,"E36"),sQuery(id+"F0.wireOp",EDGE,"E37"),sQuery(id+"F0.wireOp",EDGE,"E38"),sQuery(id+"F0.wireOp",EDGE,"E39"),sQuery(id+"F0.wireOp",EDGE,"E40"),sQuery(id+"F0.wireOp",EDGE,"E41"),sQuery(id+"F0.wireOp",EDGE,"E42"),sQuery(id+"F0.wireOp",EDGE,"E43"),sQuery(id+"F0.wireOp",EDGE,"E44"),sQuery(id+"F0.wireOp",EDGE,"E45"),sQuery(id+"F0.wireOp",EDGE,"E46"),sQuery(id+"F0.wireOp",EDGE,"E47"),sQuery(id+"F0.wireOp",EDGE,"E48"),sQuery(id+"F0.wireOp",EDGE,"E49"),sQuery(id+"F0.wireOp",EDGE,"E50"),sQuery(id+"F0.wireOp",EDGE,"E51"),sQuery(id+"F0.wireOp",EDGE,"E52"),sQuery(id+"F0.wireOp",EDGE,"E53"),sQuery(id+"F0.wireOp",EDGE,"E54"),sQuery(id+"F0.wireOp",EDGE,"E55"),sQuery(id+"F0.wireOp",EDGE,"E56"),sQuery(id+"F0.wireOp",EDGE,"E57"),sQuery(id+"F0.wireOp",EDGE,"E58"),sQuery(id+"F0.wireOp",EDGE,"E59"),sQuery(id+"F0.wireOp",EDGE,"E60"),sQuery(id+"F0.wireOp",EDGE,"E61"),sQuery(id+"F0.wireOp",EDGE,"E62"),sQuery(id+"F0.wireOp",EDGE,"E63"),sQuery(id+"F0.wireOp",EDGE,"E64"),sQuery(id+"F0.wireOp",EDGE,"E65"),sQuery(id+"F0.wireOp",EDGE,"E66"),sQuery(id+"F0.wireOp",EDGE,"E67"),sQuery(id+"F0.wireOp",EDGE,"E68"),sQuery(id+"F0.wireOp",EDGE,"E69"),sQuery(id+"F0.wireOp",EDGE,"E70"),sQuery(id+"F0.wireOp",EDGE,"E71"),sQuery(id+"F0.wireOp",EDGE,"E72"),sQuery(id+"F0.wireOp",EDGE,"E73"),sQuery(id+"F0.wireOp",EDGE,"E74"),sQuery(id+"F0.wireOp",EDGE,"E75"),sQuery(id+"F0.wireOp",EDGE,"E76"),sQuery(id+"F0.wireOp",EDGE,"E77"),sQuery(id+"F0.wireOp",EDGE,"E78"),sQuery(id+"F0.wireOp",EDGE,"E79"),sQuery(id+"F0.wireOp",EDGE,"E80"),sQuery(id+"F0.wireOp",EDGE,"E81"),sQuery(id+"F0.wireOp",EDGE,"E82"),sQuery(id+"F0.wireOp",EDGE,"E83"),sQuery(id+"F0.wireOp",EDGE,"E84"),sQuery(id+"F0.wireOp",EDGE,"E85"),sQuery(id+"F0.wireOp",EDGE,"E86"),sQuery(id+"F0.wireOp",EDGE,"E87"),sQuery(id+"F0.wireOp",EDGE,"E88"),sQuery(id+"F0.wireOp",EDGE,"E89"),sQuery(id+"F0.wireOp",EDGE,"E90"),sQuery(id+"F0.wireOp",EDGE,"E91"),sQuery(id+"F0.wireOp",EDGE,"E92"),sQuery(id+"F0.wireOp",EDGE,"E93"),sQuery(id+"F0.wireOp",EDGE,"E94"),sQuery(id+"F0.wireOp",EDGE,"E95"),sQuery(id+"F0.wireOp",EDGE,"E96"),sQuery(id+"F0.wireOp",EDGE,"E97"),sQuery(id+"F0.wireOp",EDGE,"E98"),sQuery(id+"F0.wireOp",EDGE,"E99"),sQuery(id+"F0.wireOp",EDGE,"E100"),sQuery(id+"F0.wireOp",EDGE,"E101"),sQuery(id+"F0.wireOp",EDGE,"E102"),sQuery(id+"F0.wireOp",EDGE,"E103"),sQuery(id+"F0.wireOp",EDGE,"E104"),sQuery(id+"F0.wireOp",EDGE,"E105"),sQuery(id+"F0.wireOp",EDGE,"E106"),sQuery(id+"F0.wireOp",EDGE,"E107"),sQuery(id+"F0.wireOp",EDGE,"E108"),sQuery(id+"F0.wireOp",EDGE,"E109"),sQuery(id+"F0.wireOp",EDGE,"E110"),sQuery(id+"F0.wireOp",EDGE,"E111"),sQuery(id+"F0.wireOp",EDGE,"E112"),sQuery(id+"F0.wireOp",EDGE,"E113"),sQuery(id+"F0.wireOp",EDGE,"E114"),sQuery(id+"F0.wireOp",EDGE,"E115"),sQuery(id+"F0.wireOp",EDGE,"E116"),sQuery(id+"F0.wireOp",EDGE,"E117"),sQuery(id+"F0.wireOp",EDGE,"E118"),sQuery(id+"F0.wireOp",EDGE,"E119"),sQuery(id+"F0.wireOp",EDGE,"E120"),sQuery(id+"F0.wireOp",EDGE,"E121"),sQuery(id+"F0.wireOp",EDGE,"E122"),sQuery(id+"F0.wireOp",EDGE,"E123"),sQuery(id+"F0.wireOp",EDGE,"E124"),sQuery(id+"F0.wireOp",EDGE,"E125"),sQuery(id+"F0.wireOp",EDGE,"E126"),sQuery(id+"F0.wireOp",EDGE,"E127"),sQuery(id+"F0.wireOp",EDGE,"E128"),sQuery(id+"F0.wireOp",EDGE,"E129"),sQuery(id+"F0.wireOp",EDGE,"E130"),sQuery(id+"F0.wireOp",EDGE,"E131"),sQuery(id+"F0.wireOp",EDGE,"E132"),sQuery(id+"F0.wireOp",EDGE,"E133"),sQuery(id+"F0.wireOp",EDGE,"E134"),sQuery(id+"F0.wireOp",EDGE,"E135"),sQuery(id+"F0.wireOp",EDGE,"E136"),sQuery(id+"F0.wireOp",EDGE,"E137"),sQuery(id+"F0.wireOp",EDGE,"E138"),sQuery(id+"F0.wireOp",EDGE,"E139"),sQuery(id+"F0.wireOp",EDGE,"E140"),sQuery(id+"F0.wireOp",EDGE,"E141"),sQuery(id+"F0.wireOp",EDGE,"E142"),sQuery(id+"F0.wireOp",EDGE,"E143"),sQuery(id+"F0.wireOp",EDGE,"E144"),sQuery(id+"F0.wireOp",EDGE,"E145"),sQuery(id+"F0.wireOp",EDGE,"E146"),sQuery(id+"F0.wireOp",EDGE,"E147"),sQuery(id+"F0.wireOp",EDGE,"E148"),sQuery(id+"F0.wireOp",EDGE,"E149"),sQuery(id+"F0.wireOp",EDGE,"E150"),sQuery(id+"F0.wireOp",EDGE,"E151"),sQuery(id+"F0.wireOp",EDGE,"E152"),sQuery(id+"F0.wireOp",EDGE,"E153"),sQuery(id+"F0.wireOp",EDGE,"E154"),sQuery(id+"F0.wireOp",EDGE,"E155"),sQuery(id+"F0.wireOp",EDGE,"E156"),sQuery(id+"F0.wireOp",EDGE,"E157"),sQuery(id+"F0.wireOp",EDGE,"E158"),sQuery(id+"F0.wireOp",EDGE,"E159"),sQuery(id+"F0.wireOp",EDGE,"E160"),sQuery(id+"F0.wireOp",EDGE,"E161"),sQuery(id+"F0.wireOp",EDGE,"E162"),sQuery(id+"F0.wireOp",EDGE,"E163"),sQuery(id+"F0.wireOp",EDGE,"E164"),sQuery(id+"F0.wireOp",EDGE,"E165"),sQuery(id+"F0.wireOp",EDGE,"E166"),sQuery(id+"F0.wireOp",EDGE,"E167"),sQuery(id+"F0.wireOp",EDGE,"E168"),sQuery(id+"F0.wireOp",EDGE,"E169"),sQuery(id+"F0.wireOp",EDGE,"E170"),sQuery(id+"F0.wireOp",EDGE,"E171"),sQuery(id+"F0.wireOp",EDGE,"E172"),sQuery(id+"F0.wireOp",EDGE,"E173"),sQuery(id+"F0.wireOp",EDGE,"E174"),sQuery(id+"F0.wireOp",EDGE,"E175"),sQuery(id+"F0.wireOp",EDGE,"E176"),sQuery(id+"F0.wireOp",EDGE,"E177"),sQuery(id+"F0.wireOp",EDGE,"E178"),sQuery(id+"F0.wireOp",EDGE,"E179"),sQuery(id+"F0.wireOp",EDGE,"E180"),sQuery(id+"F0.wireOp",EDGE,"E181"),sQuery(id+"F0.wireOp",EDGE,"E182"),sQuery(id+"F0.wireOp",EDGE,"E183"),sQuery(id+"F0.wireOp",EDGE,"E184"),sQuery(id+"F0.wireOp",EDGE,"E185"),sQuery(id+"F0.wireOp",EDGE,"E186"),sQuery(id+"F0.wireOp",EDGE,"E187"),sQuery(id+"F0.wireOp",EDGE,"E188"),sQuery(id+"F0.wireOp",EDGE,"E189"),sQuery(id+"F0.wireOp",EDGE,"E190"),sQuery(id+"F0.wireOp",EDGE,"E191"),sQuery(id+"F0.wireOp",EDGE,"E192"),sQuery(id+"F0.wireOp",EDGE,"E193"),sQuery(id+"F0.wireOp",EDGE,"E194"),sQuery(id+"F0.wireOp",EDGE,"E195"),sQuery(id+"F0.wireOp",EDGE,"E196"),sQuery(id+"F0.wireOp",EDGE,"E197"),sQuery(id+"F0.wireOp",EDGE,"E198"),sQuery(id+"F0.wireOp",EDGE,"E199"),sQuery(id+"F0.wireOp",EDGE,"E200"),sQuery(id+"F0.wireOp",EDGE,"E201"),sQuery(id+"F0.wireOp",EDGE,"E202"),sQuery(id+"F0.wireOp",EDGE,"E203"),sQuery(id+"F0.wireOp",EDGE,"E204"),sQuery(id+"F0.wireOp",EDGE,"E205"),sQuery(id+"F0.wireOp",EDGE,"E206"),sQuery(id+"F0.wireOp",EDGE,"E207"),sQuery(id+"F0.wireOp",EDGE,"E208"),sQuery(id+"F0.wireOp",EDGE,"E209"),sQuery(id+"F0.wireOp",EDGE,"E210"),sQuery(id+"F0.wireOp",EDGE,"E211"),sQuery(id+"F0.wireOp",EDGE,"E212"),sQuery(id+"F0.wireOp",EDGE,"E213"),sQuery(id+"F0.wireOp",EDGE,"E214"),sQuery(id+"F0.wireOp",EDGE,"E215"),sQuery(id+"F0.wireOp",EDGE,"E216"),sQuery(id+"F0.wireOp",EDGE,"E217"),sQuery(id+"F0.wireOp",EDGE,"E218"),sQuery(id+"F0.wireOp",EDGE,"E219"),sQuery(id+"F0.wireOp",EDGE,"E220"),sQuery(id+"F0.wireOp",EDGE,"E221"),sQuery(id+"F0.wireOp",EDGE,"E222"),sQuery(id+"F0.wireOp",EDGE,"E223"),sQuery(id+"F0.wireOp",EDGE,"E224"),sQuery(id+"F0.wireOp",EDGE,"E225"),sQuery(id+"F0.wireOp",EDGE,"E226"),sQuery(id+"F0.wireOp",EDGE,"E227"),sQuery(id+"F0.wireOp",EDGE,"E228"),sQuery(id+"F0.wireOp",EDGE,"E229"),sQuery(id+"F0.wireOp",EDGE,"E230"),sQuery(id+"F0.wireOp",EDGE,"E231"),sQuery(id+"F0.wireOp",EDGE,"E232"),sQuery(id+"F0.wireOp",EDGE,"E233"),sQuery(id+"F0.wireOp",EDGE,"E234"),sQuery(id+"F0.wireOp",EDGE,"E235"),sQuery(id+"F0.wireOp",EDGE,"E236"),sQuery(id+"F0.wireOp",EDGE,"E237"),sQuery(id+"F0.wireOp",EDGE,"E238"),sQuery(id+"F0.wireOp",EDGE,"E239"),sQuery(id+"F0.wireOp",EDGE,"E240"),sQuery(id+"F0.wireOp",EDGE,"E241"),sQuery(id+"F0.wireOp",EDGE,"E242"),sQuery(id+"F0.wireOp",EDGE,"E243"),sQuery(id+"F0.wireOp",EDGE,"E244"),sQuery(id+"F0.wireOp",EDGE,"E245"),sQuery(id+"F0.wireOp",EDGE,"E246"),sQuery(id+"F0.wireOp",EDGE,"E247"),sQuery(id+"F0.wireOp",EDGE,"E248"),sQuery(id+"F0.wireOp",EDGE,"E249"),sQuery(id+"F0.wireOp",EDGE,"E250"),sQuery(id+"F0.wireOp",EDGE,"E251"),sQuery(id+"F0.wireOp",EDGE,"E252"),sQuery(id+"F0.wireOp",EDGE,"E253"),sQuery(id+"F0.wireOp",EDGE,"E254"),sQuery(id+"F0.wireOp",EDGE,"E255"),sQuery(id+"F0.wireOp",EDGE,"E256"),sQuery(id+"F0.wireOp",EDGE,"E257"),sQuery(id+"F0.wireOp",EDGE,"E258"),sQuery(id+"F0.wireOp",EDGE,"E259"),sQuery(id+"F0.wireOp",EDGE,"E260"),sQuery(id+"F0.wireOp",EDGE,"E261"),sQuery(id+"F0.wireOp",EDGE,"E262"),sQuery(id+"F0.wireOp",EDGE,"E263"),sQuery(id+"F0.wireOp",EDGE,"E264"),sQuery(id+"F0.wireOp",EDGE,"E265"),sQuery(id+"F0.wireOp",EDGE,"E266"),sQuery(id+"F0.wireOp",EDGE,"E267"),sQuery(id+"F0.wireOp",EDGE,"E268"),sQuery(id+"F0.wireOp",EDGE,"E269"),sQuery(id+"F0.wireOp",EDGE,"E270"),sQuery(id+"F0.wireOp",EDGE,"E271"),sQuery(id+"F0.wireOp",EDGE,"E272"),sQuery(id+"F0.wireOp",EDGE,"E273"),sQuery(id+"F0.wireOp",EDGE,"E274"),sQuery(id+"F0.wireOp",EDGE,"E275"),sQuery(id+"F0.wireOp",EDGE,"E276"),sQuery(id+"F0.wireOp",EDGE,"E277"),sQuery(id+"F0.wireOp",EDGE,"E278"),sQuery(id+"F0.wireOp",EDGE,"E279"),sQuery(id+"F0.wireOp",EDGE,"E280"),sQuery(id+"F0.wireOp",EDGE,"E281"),sQuery(id+"F0.wireOp",EDGE,"E282"),sQuery(id+"F0.wireOp",EDGE,"E283"),sQuery(id+"F0.wireOp",EDGE,"E284"),sQuery(id+"F0.wireOp",EDGE,"E285"),sQuery(id+"F0.wireOp",EDGE,"E286"),sQuery(id+"F0.wireOp",EDGE,"E287"),sQuery(id+"F0.wireOp",EDGE,"E288"),sQuery(id+"F0.wireOp",EDGE,"E289"),sQuery(id+"F0.wireOp",EDGE,"E290"),sQuery(id+"F0.wireOp",EDGE,"E291"),sQuery(id+"F0.wireOp",EDGE,"E292"),sQuery(id+"F0.wireOp",EDGE,"E293"),sQuery(id+"F0.wireOp",EDGE,"E294"),sQuery(id+"F0.wireOp",EDGE,"E295"),sQuery(id+"F0.wireOp",EDGE,"E296"),sQuery(id+"F0.wireOp",EDGE,"E297"),sQuery(id+"F0.wireOp",EDGE,"E298"),sQuery(id+"F0.wireOp",EDGE,"E299"),sQuery(id+"F0.wireOp",EDGE,"E300"),sQuery(id+"F0.wireOp",EDGE,"E301"),sQuery(id+"F0.wireOp",EDGE,"E302"),sQuery(id+"F0.wireOp",EDGE,"E303"),sQuery(id+"F0.wireOp",EDGE,"E304"),sQuery(id+"F0.wireOp",EDGE,"E305"),sQuery(id+"F0.wireOp",EDGE,"E306"),sQuery(id+"F0.wireOp",EDGE,"E307"),sQuery(id+"F0.wireOp",EDGE,"E308"),sQuery(id+"F0.wireOp",EDGE,"E309"),sQuery(id+"F0.wireOp",EDGE,"E310"),sQuery(id+"F0.wireOp",EDGE,"E311"),sQuery(id+"F0.wireOp",EDGE,"E312"),sQuery(id+"F0.wireOp",EDGE,"E313"),sQuery(id+"F0.wireOp",EDGE,"E314"),sQuery(id+"F0.wireOp",EDGE,"E315"),sQuery(id+"F0.wireOp",EDGE,"E316"),sQuery(id+"F0.wireOp",EDGE,"E317"),sQuery(id+"F0.wireOp",EDGE,"E318"),sQuery(id+"F0.wireOp",EDGE,"E319"),sQuery(id+"F0.wireOp",EDGE,"E320"),sQuery(id+"F0.wireOp",EDGE,"E321"),sQuery(id+"F0.wireOp",EDGE,"E322"),sQuery(id+"F0.wireOp",EDGE,"E323"),sQuery(id+"F0.wireOp",EDGE,"E324"),sQuery(id+"F0.wireOp",EDGE,"E325"),sQuery(id+"F0.wireOp",EDGE,"E326"),sQuery(id+"F0.wireOp",EDGE,"E327"),sQuery(id+"F0.wireOp",EDGE,"E328"),sQuery(id+"F0.wireOp",EDGE,"E329"),sQuery(id+"F0.wireOp",EDGE,"E330"),sQuery(id+"F0.wireOp",EDGE,"E331"),sQuery(id+"F0.wireOp",EDGE,"E332"),sQuery(id+"F0.wireOp",EDGE,"E333"),sQuery(id+"F0.wireOp",EDGE,"E334"),sQuery(id+"F0.wireOp",EDGE,"E335"),sQuery(id+"F0.wireOp",EDGE,"E336"),sQuery(id+"F0.wireOp",EDGE,"E337"),sQuery(id+"F0.wireOp",EDGE,"E338"),sQuery(id+"F0.wireOp",EDGE,"E339"),sQuery(id+"F0.wireOp",EDGE,"E340"),sQuery(id+"F0.wireOp",EDGE,"E341"),sQuery(id+"F0.wireOp",EDGE,"E342"),sQuery(id+"F0.wireOp",EDGE,"E343"),sQuery(id+"F0.wireOp",EDGE,"E344"),sQuery(id+"F0.wireOp",EDGE,"E345"),sQuery(id+"F0.wireOp",EDGE,"E346"),sQuery(id+"F0.wireOp",EDGE,"E347"),sQuery(id+"F0.wireOp",EDGE,"E348"),sQuery(id+"F0.wireOp",EDGE,"E349"),sQuery(id+"F0.wireOp",EDGE,"E350"),sQuery(id+"F0.wireOp",EDGE,"E351"),sQuery(id+"F0.wireOp",EDGE,"E352"),sQuery(id+"F0.wireOp",EDGE,"E353"),sQuery(id+"F0.wireOp",EDGE,"E354"),sQuery(id+"F0.wireOp",EDGE,"E355"),sQuery(id+"F0.wireOp",EDGE,"E356"),sQuery(id+"F0.wireOp",EDGE,"E357"),sQuery(id+"F0.wireOp",EDGE,"E358"),sQuery(id+"F0.wireOp",EDGE,"E359"),sQuery(id+"F0.wireOp",EDGE,"E360"),sQuery(id+"F0.wireOp",EDGE,"E361"),sQuery(id+"F0.wireOp",EDGE,"E362"),sQuery(id+"F0.wireOp",EDGE,"E363"),sQuery(id+"F0.wireOp",EDGE,"E364"),sQuery(id+"F0.wireOp",EDGE,"E365"),sQuery(id+"F0.wireOp",EDGE,"E366"),sQuery(id+"F0.wireOp",EDGE,"E367"),sQuery(id+"F0.wireOp",EDGE,"E368"),sQuery(id+"F0.wireOp",EDGE,"E369"),sQuery(id+"F0.wireOp",EDGE,"E370"),sQuery(id+"F0.wireOp",EDGE,"E371"),sQuery(id+"F0.wireOp",EDGE,"E372"),sQuery(id+"F0.wireOp",EDGE,"E373"),sQuery(id+"F0.wireOp",EDGE,"E374"),sQuery(id+"F0.wireOp",EDGE,"E375"),sQuery(id+"F0.wireOp",EDGE,"E376"),sQuery(id+"F0.wireOp",EDGE,"E377"),sQuery(id+"F0.wireOp",EDGE,"E378"),sQuery(id+"F0.wireOp",EDGE,"E379"),sQuery(id+"F0.wireOp",EDGE,"E380"),sQuery(id+"F0.wireOp",EDGE,"E381"),sQuery(id+"F0.wireOp",EDGE,"E382"),sQuery(id+"F0.wireOp",EDGE,"E383"),sQuery(id+"F0.wireOp",EDGE,"E384"),sQuery(id+"F0.wireOp",EDGE,"E385"),sQuery(id+"F0.wireOp",EDGE,"E386"),sQuery(id+"F0.wireOp",EDGE,"E387"),sQuery(id+"F0.wireOp",EDGE,"E388"),sQuery(id+"F0.wireOp",EDGE,"E389"),sQuery(id+"F0.wireOp",EDGE,"E390"),sQuery(id+"F0.wireOp",EDGE,"E391"),sQuery(id+"F0.wireOp",EDGE,"E392"),sQuery(id+"F0.wireOp",EDGE,"E393"),sQuery(id+"F0.wireOp",EDGE,"E394"),sQuery(id+"F0.wireOp",EDGE,"E395"),sQuery(id+"F0.wireOp",EDGE,"E396"),sQuery(id+"F0.wireOp",EDGE,"E397"),sQuery(id+"F0.wireOp",EDGE,"E398"),sQuery(id+"F0.wireOp",EDGE,"E399"),sQuery(id+"F0.wireOp",EDGE,"E400"),sQuery(id+"F0.wireOp",EDGE,"E401"),sQuery(id+"F0.wireOp",EDGE,"E402"),sQuery(id+"F0.wireOp",EDGE,"E403"),sQuery(id+"F0.wireOp",EDGE,"E404"),sQuery(id+"F0.wireOp",EDGE,"E405"),sQuery(id+"F0.wireOp",EDGE,"E406"),sQuery(id+"F0.wireOp",EDGE,"E407"),sQuery(id+"F0.wireOp",EDGE,"E408"),sQuery(id+"F0.wireOp",EDGE,"E409"),sQuery(id+"F0.wireOp",EDGE,"E410"),sQuery(id+"F0.wireOp",EDGE,"E411"),sQuery(id+"F0.wireOp",EDGE,"E412"),sQuery(id+"F0.wireOp",EDGE,"E413"),sQuery(id+"F0.wireOp",EDGE,"E414"),sQuery(id+"F0.wireOp",EDGE,"E415"),sQuery(id+"F0.wireOp",EDGE,"E416"),sQuery(id+"F0.wireOp",EDGE,"E417"),sQuery(id+"F0.wireOp",EDGE,"E418"),sQuery(id+"F0.wireOp",EDGE,"E419"),sQuery(id+"F0.wireOp",EDGE,"E420"),sQuery(id+"F0.wireOp",EDGE,"E421"),sQuery(id+"F0.wireOp",EDGE,"E422"),sQuery(id+"F0.wireOp",EDGE,"E423"),sQuery(id+"F0.wireOp",EDGE,"E424"),sQuery(id+"F0.wireOp",EDGE,"E425"),sQuery(id+"F0.wireOp",EDGE,"E426"),sQuery(id+"F0.wireOp",EDGE,"E427"),sQuery(id+"F0.wireOp",EDGE,"E428"),sQuery(id+"F0.wireOp",EDGE,"E429"),sQuery(id+"F0.wireOp",EDGE,"E430"),sQuery(id+"F0.wireOp",EDGE,"E431"),sQuery(id+"F0.wireOp",EDGE,"E432"),sQuery(id+"F0.wireOp",EDGE,"E433"),sQuery(id+"F0.wireOp",EDGE,"E434"),sQuery(id+"F0.wireOp",EDGE,"E435"),sQuery(id+"F0.wireOp",EDGE,"E436"),sQuery(id+"F0.wireOp",EDGE,"E437"),sQuery(id+"F0.wireOp",EDGE,"E438"),sQuery(id+"F0.wireOp",EDGE,"E439"),sQuery(id+"F0.wireOp",EDGE,"E440"),sQuery(id+"F0.wireOp",EDGE,"E441"),sQuery(id+"F0.wireOp",EDGE,"E442"),sQuery(id+"F0.wireOp",EDGE,"E443"),sQuery(id+"F0.wireOp",EDGE,"E444"),sQuery(id+"F0.wireOp",EDGE,"E445"),sQuery(id+"F0.wireOp",EDGE,"E446"),sQuery(id+"F0.wireOp",EDGE,"E447"),sQuery(id+"F0.wireOp",EDGE,"E448"),sQuery(id+"F0.wireOp",EDGE,"E449"),sQuery(id+"F0.wireOp",EDGE,"E450")])]});
            var Q1;
            Q1=makeQuery(id+"F1.opExtrude","CAP_VERTEX",VERTEX,{"disambiguationData":[OSD([sQuery(id+"F0.wireOp",EDGE,"E171"),sQuery(id+"F0.wireOp",EDGE,"E172")])],"isStart":false});
            transform(context, id + "F4", {"entities" : qUnion([Q0]), "transformType" : TransformType.SCALE_UNIFORMLY, "scale" : 10, "scalePoint" : qUnion([Q1]), "makeCopy" : false});
        }
    });
